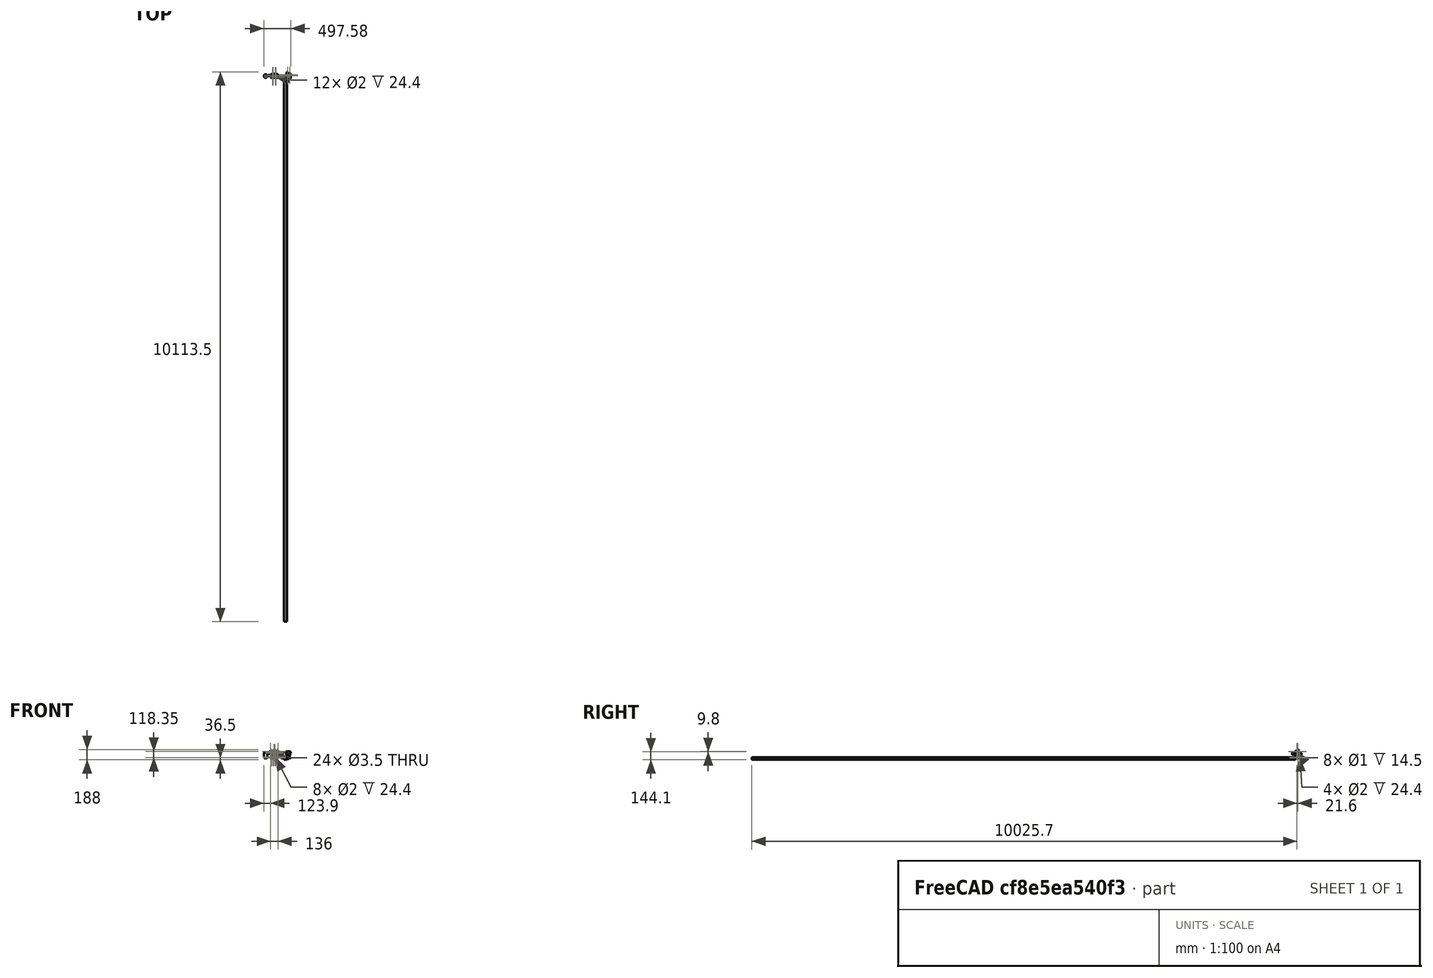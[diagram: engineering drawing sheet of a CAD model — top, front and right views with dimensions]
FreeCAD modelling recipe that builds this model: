
FCSTD DOCUMENT  (FreeCAD 0.15R4671 (Git))
Label: darth void
License: All rights reserved
LicenseURL: http://es.wikipedia.org/wiki/Todos_los_derechos_reservados
objects: Part::Feature×135, Part::Cylinder×55, Part::Cut×53, Part::Box×41, Part::MultiFuse×36, Sketcher::SketchObject×14, Part::FeaturePython×14, App::DocumentObjectGroup×10, Part::Mirroring×9, Part::Fillet×9, PartDesign::Pad×9, Part::Chamfer×6, PartDesign::Pocket×5, Part::Prism×3, Mesh::Feature×3, PartDesign::Fillet×2
note: 405 computed .brp shape members not serialized (recipe doc carries the construction recipe); baked Part::Feature solids carry a one-line shape summary decoded from their .brp

FEATURE [Part::Feature] Part__Feature  label="Servo-D1"
  Placement = pos=(26.5,9.5,100.6) rot=(0,1,0;3.14159rad)
  shape: bbox 55.5 x 20 x 41.74 mm, 365 faces (baked)
FEATURE [Part::Feature] Part__Feature001  label="Servo-D2"
  Placement = pos=(0,0,13) rot=(0.57735,0.57735,0.57735;2.0944rad)
  shape: bbox 41.74 x 55.5 x 20 mm, 365 faces (baked)
FEATURE [Part::Feature] Part__Feature002  label="J1"
  Placement = pos=(-10.8,44.37,77.54) rot=(0.707107,0.707107,0;3.14159rad)
  shape: bbox 11.7 x 15.49 x 2.5 mm, 224 faces (baked)
FEATURE [Part::Feature] Part__Feature003  label="J2"
  Placement = pos=(-10.8,62.15,77.54) rot=(0.707107,0.707107,0;3.14159rad)
  shape: bbox 11.7 x 15.49 x 2.5 mm, 224 faces (baked)
FEATURE [Part::Feature] Part__Feature004  label="J4"
  Placement = pos=(-10.8,59.6199,125.78) rot=(0,0,-1;1.5708rad)
  shape: bbox 11.65 x 20.57 x 2.5 mm, 290 faces (baked)
FEATURE [Part::Feature] Part__Feature005  label="J16"
  Placement = pos=(-9.55,7.19908,100.417) rot=(0.57735,0.57735,-0.57735;2.0944rad)
  shape: bbox 2.94 x 5.43 x 7.98 mm, 414 faces, 0 solids (baked)
FEATURE [Part::Feature] Part__Feature006  label="PCB"
  Placement = pos=(-12.3914,5,75) rot=(0.57735,0.57735,0.57735;2.0944rad)
  shape: bbox 1.591 x 68.6 x 53.36 mm, 426 faces (baked)
FEATURE [Part::Feature] Part__Feature007  label="J010"
  Placement = pos=(-10.8,14.8841,83.3059) rot=(0.707107,0.707107,0;3.14159rad)
  shape: bbox 10.92 x 14.61 x 8.89 mm, 41 faces (baked)
FEATURE [Part::Feature] Part__Feature008  label="U1"
  Placement = pos=(-9.2,12.159,115.511) rot=(0.57735,-0.57735,-0.57735;2.0944rad)
  shape: bbox 2.435 x 26.9 x 13 mm, 503 faces (baked)
FEATURE [Part::Feature] Part__Feature009  label="J8"
  Placement = pos=(-10.8,37.7759,125.78) rot=(0,0,-1;1.5708rad)
  shape: bbox 11.65 x 20.57 x 2.5 mm, 290 faces (baked)
FEATURE [App::DocumentObjectGroup] Group  label="placa"
  Group = -> [Part__Feature002,Part__Feature003,Part__Feature004,Part__Feature005,Part__Feature006,Part__Feature007,Part__Feature008,Part__Feature009]
FEATURE [Part::Box] Box  label="Cube"
  Height = 24
  Length = 72
  Placement = pos=(-15,-29,-3) rot=(0,0,1;0rad)
  Width = 58
FEATURE [Part::Box] Box001  label="Cube001"
  Height = 25
  Length = 47
  Placement = pos=(-1,-21,2) rot=(0,0,1;0rad)
  Width = 42
FEATURE [Part::Box] Box002  label="Cube002"
  Height = 38
  Length = 28
  Placement = pos=(37,-45,1) rot=(0,0,1;0rad)
  Width = 88
FEATURE [Part::Box] Box003  label="Cube003"
  Height = 38
  Length = 28
  Placement = pos=(-33,-45,1) rot=(0,0,1;0rad)
  Width = 88
FEATURE [Part::Cut] Cut
  Base = -> Box
  Tool = -> Box001
FEATURE [Part::Cut] Cut001
  Base = -> Cut
  Tool = -> Box002
FEATURE [Part::Cut] Cut002
  Base = -> Cut001
  Tool = -> Box003
FEATURE [Part::Box] Box004  label="Cube004"
  Height = 60
  Length = 44
  Placement = pos=(-5,-24,-5) rot=(0,0,1;0rad)
  Width = 61
FEATURE [Part::Mirroring] Part__Mirroring  label="Servo-D1 (Mirror #1)"
  Base = (0,0,0)
  Normal = (0,1,0)
  Placement = pos=(0,72,0) rot=(0,0,1;0rad)
  Source = -> Part__Feature
FEATURE [Part::Mirroring] Part__Mirroring001  label="Servo-D2 (Mirror #2)"
  Base = (0,0,0)
  Normal = (0,1,0)
  Placement = pos=(0,72,0) rot=(0,0,1;0rad)
  Source = -> Part__Feature001
FEATURE [Part::Cylinder] Cylinder  label="Joint-D005"
  Angle = 360
  Height = 74.5
  Placement = pos=(-22,9.5,12) rot=(0,1,0;1.5708rad)
  Radius = 1.75
FEATURE [Part::Fillet] Fillet
  Base = -> Cut002
  Edges = 4 edges r=10: [Edge1,Edge3,Edge5,Edge14]
FEATURE [Part::Cylinder] Cylinder001  label="Joint-D004"
  Angle = 360
  Height = 53
  Placement = pos=(-9,9.5,12) rot=(0,1,0;1.5708rad)
  Radius = 10.5
FEATURE [Part::MultiFuse] Fusion
  Shapes = -> [Cylinder001]
FEATURE [Part::Cylinder] Cylinder002  label="Joint-D006"
  Angle = 360
  Height = 74.5
  Placement = pos=(16,9.5,12) rot=(0,1,0;1.5708rad)
  Radius = 5.5
FEATURE [Part::Cut] Cut003
  Base = -> Fusion
  Tool = -> Box004
FEATURE [Part::Cylinder] Cylinder003  label="Joint-D007"
  Angle = 360
  Height = 74.5
  Placement = pos=(-51,9.5,12) rot=(0,1,0;1.5708rad)
  Radius = 1.75
FEATURE [Part::Cut] Cut004
  Base = -> Cut003
  Tool = -> Cylinder002
FEATURE [Part::Cut] Cut005
  Base = -> Cut004
  Tool = -> Cylinder003
FEATURE [Part::Cylinder] Cylinder004  label="Joint-D008"
  Angle = 360
  Height = 74.5
  Placement = pos=(41.8,9.5,12) rot=(0,1,0;1.5708rad)
  Radius = 11
FEATURE [Part::Cut] Cut006
  Base = -> Cut005
  Tool = -> Cylinder004
FEATURE [Part::Cylinder] Cylinder005  label="Joint-D009"
  Angle = 360
  Height = 23.5
  Placement = pos=(16.8,9.5,58.3) rot=(0,1,0;3.14159rad)
  Radius = 11
FEATURE [Part::Cylinder] Cylinder006  label="Joint-D010"
  Angle = 360
  Height = 21.5
  Placement = pos=(16,-24.5,7) rot=(0,1,0;1.5708rad)
  Radius = 1.75
FEATURE [Part::Cylinder] Cylinder007  label="Joint-D011"
  Angle = 360
  Height = 21.5
  Placement = pos=(32,-24.5,7) rot=(0,1,0;1.5708rad)
  Radius = 3
FEATURE [Part::MultiFuse] Fusion001
  Shapes = -> [Cylinder007,Cylinder006]
FEATURE [Part::MultiFuse] Fusion002
  Placement = pos=(0,0,10) rot=(0,0,1;0rad)
  Shapes = -> [Cylinder007,Cylinder006]
FEATURE [Part::MultiFuse] Fusion003
  Placement = pos=(0,49,0) rot=(0,0,1;0rad)
  Shapes = -> [Cylinder007,Cylinder006]
FEATURE [Part::MultiFuse] Fusion004
  Placement = pos=(0,49,10) rot=(0,0,1;0rad)
  Shapes = -> [Cylinder007,Cylinder006]
FEATURE [Part::Box] Box005  label="Cube006"
  Height = 21
  Length = 4
  Placement = pos=(25.5,-28,2) rot=(0,0,1;0rad)
  Width = 56
FEATURE [Part::Cylinder] Cylinder008  label="Joint-D012"
  Angle = 360
  Height = 74.5
  Placement = pos=(17,9.5,12) rot=(0,0,1;0rad)
  Radius = 5.5
FEATURE [Part::Box] Box006  label="Cube007"
  Height = 6
  Length = 3
  Placement = pos=(18.5,-28,4) rot=(0,0,1;0rad)
  Width = 56
FEATURE [Part::Box] Box007  label="Cube008"
  Height = 6
  Length = 3
  Placement = pos=(18.5,-28,14) rot=(0,0,1;0rad)
  Width = 56
FEATURE [Part::Cylinder] Cylinder009  label="Joint-D013"
  Angle = 360
  Height = 74.5
  Placement = pos=(-3,9.5,12) rot=(0,1,0;1.5708rad)
  Radius = 2.75
FEATURE [Part::Box] Box008  label="Cube009"
  Height = 5
  Length = 80
  Placement = pos=(-23,-4,63) rot=(0,0,1;0rad)
  Width = 80
FEATURE [Part::Box] Box009  label="Cube010"
  Height = 9
  Length = 7
  Placement = pos=(-1,-1,63) rot=(0,0,1;0rad)
  Width = 74
FEATURE [Part::Box] Box010  label="Cube011"
  Height = 9
  Length = 7
  Placement = pos=(47,-1,63) rot=(0,0,1;0rad)
  Width = 74
FEATURE [Part::MultiFuse] Fusion005
  Placement = pos=(44,39,98) rot=(0,1,0;1.5708rad)
  Shapes = -> [Cylinder007,Cylinder006]
FEATURE [Part::MultiFuse] Fusion006
  Placement = pos=(44,29,98) rot=(0,1,0;1.5708rad)
  Shapes = -> [Cylinder007,Cylinder006]
FEATURE [Part::MultiFuse] Fusion007
  Placement = pos=(-5,39,98) rot=(0,1,0;1.5708rad)
  Shapes = -> [Cylinder007,Cylinder006]
FEATURE [Part::MultiFuse] Fusion008
  Placement = pos=(-5,29,98) rot=(0,1,0;1.5708rad)
  Shapes = -> [Cylinder007,Cylinder006]
FEATURE [Part::Box] Box011  label="Cube012"
  Height = 9
  Length = 70
  Placement = pos=(-6,8.5,70) rot=(0,0,1;0rad)
  Width = 2
FEATURE [Part::MultiFuse] Fusion009
  Shapes = -> [Box011,Fusion007,Fusion008,Fusion006,Fusion005]
FEATURE [Part::MultiFuse] Fusion010
  Placement = pos=(0,53,0) rot=(0,0,1;0rad)
  Shapes = -> [Box011,Fusion007,Fusion008,Fusion006,Fusion005]
FEATURE [Part::MultiFuse] Fusion011
  Shapes = -> [Box008,Box010,Box009]
FEATURE [Part::Cut] Cut016
  Base = -> Fusion011
  Tool = -> Fusion010
FEATURE [Part::Cut] Cut017
  Base = -> Cut016
  Tool = -> Fusion009
FEATURE [Part::Box] Box012  label="Cube014"
  Height = 43
  Length = 41
  Placement = pos=(6,-1,59) rot=(0,0,1;0rad)
  Width = 21
FEATURE [Part::Box] Box013  label="Cube015"
  Height = 43
  Length = 41
  Placement = pos=(6,52,59) rot=(0,0,1;0rad)
  Width = 21
FEATURE [Part::Cut] Cut018
  Base = -> Cut017
  Tool = -> Box012
FEATURE [Part::Cut] Cut019
  Base = -> Cut018
  Tool = -> Box013
FEATURE [Part::Box] Box014  label="Cube016"
  Height = 12
  Length = 6
  Placement = pos=(-11.5,3,69) rot=(0,0,1;0rad)
  Width = 3
FEATURE [Part::Box] Box015  label="Cube017"
  Height = 12
  Length = 16
  Placement = pos=(-20,-1,63) rot=(0,0,1;0rad)
  Width = 74
FEATURE [Part::Box] Box016  label="Cube018"
  Height = 12
  Length = 6
  Placement = pos=(-11.5,66,69) rot=(0,0,1;0rad)
  Width = 3
FEATURE [Part::MultiFuse] Fusion012
  Shapes = -> [Cut019,Box015]
FEATURE [Part::Cut] Cut020
  Base = -> Fusion012
  Tool = -> Box014
FEATURE [Part::Cut] Cut021
  Base = -> Cut020
  Tool = -> Box016
FEATURE [PartDesign::Fillet] Fillet001  label="horn"
  Placement = pos=(38.5,9.5,13) rot=(0,0,-1;1.5708rad)
  Radius = 0.5
FEATURE [Part::Cylinder] Cylinder010  label="Joint-D014"
  Angle = 360
  Height = 52.5
  Placement = pos=(19,9.5,20.35) rot=(0,1,0;1.5708rad)
  Radius = 1
FEATURE [Part::Cylinder] Cylinder011  label="Joint-D015"
  Angle = 360
  Height = 52.5
  Placement = pos=(19,2,9.5) rot=(0,1,0;1.5708rad)
  Radius = 1
FEATURE [Part::Cylinder] Cylinder012  label="Joint-D016"
  Angle = 360
  Height = 52.5
  Placement = pos=(19,17,9.5) rot=(0,1,0;1.5708rad)
  Radius = 1
FEATURE [Part::MultiFuse] Fusion013
  Placement = pos=(0,0,-1) rot=(0,0,1;0rad)
  Shapes = -> [Cylinder011,Cylinder010,Cylinder012]
FEATURE [Part::MultiFuse] Fusion014
  Placement = pos=(4,0,101) rot=(0,1,0;1.5708rad)
  Shapes = -> [Cylinder011,Cylinder010,Cylinder012]
FEATURE [PartDesign::Fillet] Fillet002  label="horn001"
  Placement = pos=(16.8,9.5,62.5) rot=(-0.57735,0.57735,-0.57735;2.0944rad)
  Radius = 0.5
FEATURE [Part::Mirroring] Part__Mirroring002  label="horn (Mirror #4)"
  Base = (41.6,1.90735e-06,13)
  Normal = (0,1,-1.19209e-07)
  Placement = pos=(0,72,0) rot=(0,0,1;0rad)
  Source = -> Fillet001
FEATURE [Part::Mirroring] Part__Mirroring003  label="horn001 (Mirror #5)"
  Base = (16.8,7.62939e-06,59.3998)
  Normal = (0,1,-1.19209e-07)
  Placement = pos=(0,72,0) rot=(0,0,1;0rad)
  Source = -> Fillet002
FEATURE [Part::Chamfer] Chamfer
  Base = -> Fillet
  Edges = 3 edges r=3: [Edge18,Edge33,Edge37]
FEATURE [Part::Cut] Cut007
  Base = -> Chamfer
  Tool = -> Cylinder
FEATURE [Part::Cut] Cut008
  Base = -> Cut007
  Tool = -> Box005
FEATURE [Part::Cut] Cut009
  Base = -> Cut008
  Tool = -> Box007
FEATURE [Part::Cut] Cut010
  Base = -> Cut009
  Tool = -> Box006
FEATURE [Part::Cut] Cut011
  Base = -> Cut010
  Tool = -> Fusion004
FEATURE [Part::Cut] Cut012
  Base = -> Cut011
  Tool = -> Fusion003
FEATURE [Part::Cut] Cut013
  Base = -> Cut012
  Tool = -> Fusion002
FEATURE [Part::Cut] Cut014
  Base = -> Cut013
  Tool = -> Fusion001
FEATURE [Part::Cut] Cut015  label="pie"
  Base = -> Cut014
  Tool = -> Cylinder009
FEATURE [Part::Box] Box017  label="Cube024"
  Height = 23
  Length = 6
  Placement = pos=(0,19,7) rot=(0,0,1;0rad)
  Width = 36
FEATURE [Part::Cut] Cut022  label="pie-D"
  Base = -> Cut015
  Placement = pos=(0,0,1) rot=(0,0,1;0rad)
  Tool = -> Box017
FEATURE [Part::Mirroring] Part__Mirroring004  label="pie-I"
  Base = (0,0,0)
  Normal = (0,1,0)
  Placement = pos=(0,72,0) rot=(0,0,1;0rad)
  Source = -> Cut022
FEATURE [Part::Cut] Cut023
  Base = -> Cut006
  Tool = -> Box004
FEATURE [Part::Cut] Cut024
  Base = -> Cut023
  Tool = -> Cylinder005
FEATURE [Part::Cut] Cut025
  Base = -> Cut024
  Tool = -> Fusion014
FEATURE [Part::Cut] Cut026
  Base = -> Cut025
  Tool = -> Fusion013
FEATURE [Part::Cut] Cut027
  Base = -> Cut026
  Placement = pos=(0,0,1) rot=(0,0,1;0rad)
  Tool = -> Cylinder008
FEATURE [Part::Chamfer] Chamfer001
  Base = -> Cut027
  Edges = 1 edges r=4: [Edge61]
FEATURE [Part::Chamfer] Chamfer002  label="pata-D"
  Base = -> Chamfer001
  Edges = 1 edges r=8: [Edge58]
FEATURE [Part::Mirroring] Part__Mirroring005  label="pata-I"
  Base = (17.5,3.8147e-06,32.25)
  Normal = (0,1,-1.19209e-07)
  Placement = pos=(0,72,0) rot=(0,0,1;0rad)
  Source = -> Chamfer002
FEATURE [Part::Cylinder] Cylinder013  label="Cylinder055"
  Angle = 360
  Height = 31
  Placement = pos=(-8.5,92,71.5) rot=(1,0,0;1.5708rad)
  Radius = 1.75
FEATURE [Part::Cut] Cut028
  Base = -> Cut021
  Tool = -> Cylinder013
FEATURE [Part::Cylinder] Cylinder014  label="Cylinder001"
  Angle = 360
  Height = 31
  Placement = pos=(-8.5,11,71.5) rot=(1,0,0;1.5708rad)
  Radius = 1.75
FEATURE [Part::Feature] Part__Feature010  label="Portapilas008"
  shape: bbox 2e-07 x 47.97 x 51.59 mm, 1 faces, 0 solids (baked)
FEATURE [Part::Feature] Part__Feature011  label="Portapilas007"
  shape: bbox 9.213 x 1.1 x 48.01 mm, 3 faces, 0 solids (baked)
FEATURE [Part::Feature] Part__Feature012  label="Portapilas006"
  shape: bbox 9.213 x 1.1 x 48.01 mm, 3 faces, 0 solids (baked)
FEATURE [Part::Feature] Part__Feature013  label="Portapilas005"
  shape: bbox 9.213 x 1.1 x 48.01 mm, 3 faces, 0 solids (baked)
FEATURE [Part::Feature] Part__Feature014  label="Portapilas004"
  shape: bbox 9.213 x 1.1 x 48.01 mm, 3 faces, 0 solids (baked)
FEATURE [Part::Feature] Part__Feature015  label="Portapilas003"
  shape: bbox 9.213 x 1.1 x 48.01 mm, 3 faces, 0 solids (baked)
FEATURE [Part::Feature] Part__Feature016  label="Portapilas002"
  shape: bbox 9.213 x 1.1 x 48.01 mm, 3 faces, 0 solids (baked)
FEATURE [Part::Feature] Part__Feature017  label="Portapilas001"
  shape: bbox 16.42 x 48.04 x 51.59 mm, 26 faces, 0 solids (baked)
FEATURE [Part::Feature] Part__Feature018  label="Portapilas"
  shape: bbox 21.03 x 69.14 x 72.63 mm, 394 faces, 0 solids (baked)
FEATURE [Part::MultiFuse] Fusion015  label="peterpilas"
  Placement = pos=(23,77.5,76) rot=(0,0,1;1.5708rad)
  Shapes = -> [Part__Feature018,Part__Feature017,Part__Feature016,Part__Feature015,Part__Feature014,Part__Feature013,Part__Feature012,Part__Feature011,Part__Feature010]
FEATURE [Part::Feature] Part__Feature019  label="Ultrasonido_BAT"
  Placement = pos=(-17,36,59.5) rot=(0,0,1;0rad)
  shape: bbox 18.72 x 56 x 27.52 mm, 81 faces (baked)
FEATURE [Part::Cut] Cut029
  Base = -> Cut028
  Tool = -> Cylinder014
FEATURE [Part::Box] Box018  label="Cube032"
  Height = 20
  Length = 3
  Placement = pos=(51,20,66) rot=(0,0,1;0rad)
  Width = 32
FEATURE [Part::Box] Box019  label="Cube033"
  Height = 54
  Length = 4.5
  Placement = pos=(-20,6,64) rot=(0,0,1;0rad)
  Width = 60
FEATURE [Part::Box] Box020  label="Cube035"
  Height = 68
  Length = 6
  Placement = pos=(-23.5,17,68) rot=(0,0,1;0rad)
  Width = 38
FEATURE [Part::Box] Box021  label="Cube034"
  Height = 17
  Length = 13
  Placement = pos=(-14,20,62) rot=(0,0,1;0rad)
  Width = 32
FEATURE [Part::Fillet] Fillet003
  Base = -> Box021
  Edges = 4 edges r=5: [Edge1,Edge3,Edge5,Edge7]
FEATURE [Part::Cylinder] Cylinder015  label="Cylinder093"
  Angle = 360
  Height = 31
  Placement = pos=(-49.5,29,111.5) rot=(0,1,0;1.5708rad)
  Radius = 1.75
FEATURE [Part::Cylinder] Cylinder016  label="Cylinder094"
  Angle = 360
  Height = 31
  Placement = pos=(-49.5,49,91.5) rot=(0,1,0;1.5708rad)
  Radius = 1.75
FEATURE [Part::Cylinder] Cylinder017  label="Cylinder095"
  Angle = 360
  Height = 31
  Placement = pos=(-49.5,49,111.5) rot=(0,1,0;1.5708rad)
  Radius = 1.75
FEATURE [Part::MultiFuse] Fusion016
  Shapes = -> [Box018,Cut029]
FEATURE [Part::Box] Box022  label="Cube036"
  Height = 44
  Length = 61
  Placement = pos=(-9,22,66) rot=(0,0,1;0rad)
  Width = 28
FEATURE [Part::MultiFuse] Fusion017
  Shapes = -> [Fusion016,Box019]
FEATURE [Part::Cut] Cut030
  Base = -> Fusion017
  Tool = -> Fillet003
FEATURE [Part::Box] Box023  label="Cube037"
  Height = 11
  Length = 8
  Placement = pos=(-11.5,-52,95) rot=(0,0,1;0rad)
  Width = 58
FEATURE [Part::Cylinder] Cylinder018  label="Cylinder096"
  Angle = 360
  Height = 61
  Placement = pos=(-5,124,89.6) rot=(1,0,0;1.5708rad)
  Radius = 4
FEATURE [Part::Cylinder] Cylinder019  label="Cylinder097"
  Angle = 360
  Height = 63
  Placement = pos=(-3,11,83.5) rot=(1,0,0;1.5708rad)
  Radius = 6
FEATURE [Part::Box] Box024  label="Cube038"
  Height = 66
  Length = 76
  Placement = pos=(-21,-2,63) rot=(0,0,1;0rad)
  Width = 76
FEATURE [Part::Cylinder] Cylinder020  label="Cylinder098"
  Angle = 360
  Height = 23
  Placement = pos=(-8.5,1,71.5) rot=(1,0,0;1.5708rad)
  Radius = 1.75
FEATURE [Part::Cylinder] Cylinder021  label="Cylinder099"
  Angle = 360
  Height = 31
  Placement = pos=(-8.5,94,71.5) rot=(1,0,0;1.5708rad)
  Radius = 1.75
FEATURE [Part::Fillet] Fillet004
  Base = -> Box024
  Edges = 8 edges r=3: [Edge1,Edge2,Edge3,Edge5,Edge6,Edge7,Edge10,Edge12]
FEATURE [Part::Box] Box025  label="Cube039"
  Height = 6
  Length = 81
  Placement = pos=(-23.5,-4.5,63) rot=(0,0,1;0rad)
  Width = 81
FEATURE [Part::Fillet] Fillet005
  Base = -> Box025
  Edges = 4 edges r=5: [Edge1,Edge3,Edge5,Edge7]
  Placement = pos=(0,0,-1) rot=(0,0,1;0rad)
FEATURE [Part::Cylinder] Cylinder022  label="Cylinder100"
  Angle = 360
  Height = 45
  Placement = pos=(-8.5,-7,71.5) rot=(1,0,0;1.5708rad)
  Radius = 4
FEATURE [Part::Cylinder] Cylinder023  label="Cylinder101"
  Angle = 360
  Height = 45
  Placement = pos=(-8.5,124,71.5) rot=(1,0,0;1.5708rad)
  Radius = 4
FEATURE [Part::MultiFuse] Fusion018
  Shapes = -> [Fillet004,Fillet005]
FEATURE [Part::MultiFuse] Fusion019  label="corte-positivo"
  Shapes = -> [Fusion018,Cylinder018,Cylinder023,Cylinder021,Cylinder022,Cylinder019,Box023,Cylinder020]
FEATURE [Part::Cylinder] Cylinder024  label="Cylinder102"
  Angle = 360
  Height = 31
  Placement = pos=(-49.5,29,91.5) rot=(0,1,0;1.5708rad)
  Radius = 1.75
FEATURE [Part::MultiFuse] Fusion020
  Placement = pos=(14,0,0) rot=(0,0,1;0rad)
  Shapes = -> [Cylinder024,Cylinder016,Cylinder017,Cylinder015]
FEATURE [App::DocumentObjectGroup] Group002  label="electronic"
  Group = -> [Part__Mirroring,Part__Mirroring001,Part__Mirroring002,Part__Mirroring003,Fusion015,Part__Feature019,Group]
FEATURE [App::DocumentObjectGroup] Group003  label="aux"
  Group = -> [Fusion019]
FEATURE [Part::Cut] Cut031
  Base = -> Cut030
  Tool = -> Box022
FEATURE [Part::Chamfer] Chamfer003
  Base = -> Cut031
  Edges = 1 edges r=3: [Edge86]
FEATURE [Sketcher::SketchObject] Sketch
  Placement = pos=(-22,0,0) rot=(0.57735,-0.57735,-0.57735;2.0944rad)
  sketch-geometry (4):
    g0: ArcOfCircle CenterX=-49 CenterY=111.5 CenterZ=0 NormalX=0 NormalY=0 NormalZ=1 Radius=3.5 StartAngle=9.1497e-08 EndAngle=3.14159
    g1: LineSegment StartX=-52.5 StartY=111.5 StartZ=0 EndX=-52.5 EndY=91.5 EndZ=0
    g2: LineSegment StartX=-45.5 StartY=111.5 StartZ=0 EndX=-45.5 EndY=91.5 EndZ=0
    g3: ArcOfCircle CenterX=-49 CenterY=91.5 CenterZ=0 NormalX=0 NormalY=0 NormalZ=1 Radius=3.5 StartAngle=3.14159 EndAngle=6.28319
  constraints (13):
    c: DistanceX(g-1,g0) = -49
    c: DistanceY(g-1,g0) = 111.5
    c: Radius(g0) = 3.5
    c: Vertical(g1)
    c: Vertical(g2)
    c: Coincident(g1,g0)
    c: Coincident(g2,g0)
    c: Tangent(g2,g0)
    c: Tangent(g1,g0)
    c: Coincident(g3,g1)
    c: Coincident(g3,g2)
    c: Equal(g3,g0)
    c: Distance(g3,g0) = 20
FEATURE [PartDesign::Pad] Pad
  Length = 5
  Length2 = 100
  Placement = pos=(-22,0,0) rot=(0.57735,-0.57735,-0.57735;2.0944rad)
  Reversed = true
  Sketch = -> Sketch
  Type = 0
FEATURE [Part::FeaturePython] Clone001  label="Clone of Pad"  # Draft clone (typed FeaturePython)
  Objects = -> [Pad]
  Placement = pos=(-22,-20,0) rot=(0.57735,-0.57735,-0.57735;2.0944rad)
  Scale = (1,1,1)
FEATURE [Part::MultiFuse] Fusion021
  Placement = pos=(4.5,0,0) rot=(0,0,1;0rad)
  Shapes = -> [Pad,Clone001]
FEATURE [Part::MultiFuse] Fusion022
  Shapes = -> [Chamfer003,Fusion021]
FEATURE [Part::Cut] Cut032
  Base = -> Fusion022
  Tool = -> Fusion020
FEATURE [Part::Cut] Cut033
  Base = -> Cut032
  Tool = -> Box020
FEATURE [Sketcher::SketchObject] Sketch001  label="leg-sketch-1"
  Placement = pos=(0,0,0) rot=(0.57735,0.57735,0.57735;2.0944rad)
  sketch-geometry (5):
    g0: LineSegment StartX=-49 StartY=10.5 StartZ=0 EndX=0 EndY=10.5 EndZ=0
    g1: LineSegment StartX=0 StartY=10.5 StartZ=0 EndX=0 EndY=-10.5 EndZ=0
    g2: LineSegment StartX=0 StartY=-10.5 StartZ=0 EndX=-49 EndY=-10.5 EndZ=0
    g3: LineSegment [constr] StartX=-49 StartY=-10.5 StartZ=0 EndX=-49 EndY=10.5 EndZ=0
    g4: ArcOfCircle CenterX=-49 CenterY=0 CenterZ=0 NormalX=0 NormalY=0 NormalZ=1 Radius=10.5 StartAngle=1.5708 EndAngle=4.71239
  constraints (15):
    c: Coincident(g0,g1)
    c: Coincident(g1,g2)
    c: Coincident(g2,g3)
    c: Coincident(g3,g0)
    c: Horizontal(g0)
    c: Horizontal(g2)
    c: Vertical(g1)
    c: Vertical(g3)
    c: PointOnObject(g4,g3)
    c: Coincident(g4,g0)
    c: Coincident(g4,g2)
    c: PointOnObject(g4,g-1)
    c: PointOnObject(g0,g-2)
    c: DistanceX(g0) = 49
    c: DistanceY(g1) = -21
FEATURE [PartDesign::Pad] Pad001  label="leg-block-1"
  Length = 53
  Length2 = 100
  Midplane = true
  Placement = pos=(0,0,0) rot=(0.57735,0.57735,0.57735;2.0944rad)
  Sketch = -> Sketch001
  Type = 0
FEATURE [Sketcher::SketchObject] Sketch002  label="leg-top-sketch"
  ExternalGeometry = -> [Pad001]
  Placement = pos=(0,0,10.5) rot=(0,0,-1;1.5708rad)
  Support = -> Pad001 [Face1]
  sketch-geometry (9):
    g0: LineSegment StartX=64 StartY=21.5 StartZ=0 EndX=10 EndY=21.5 EndZ=0
    g1: LineSegment StartX=6 StartY=17.5 StartZ=0 EndX=6 EndY=-19.5 EndZ=0
    g2: LineSegment StartX=9 StartY=-22.5 StartZ=0 EndX=64 EndY=-22.5 EndZ=0
    g3: LineSegment StartX=64 StartY=-22.5 StartZ=0 EndX=64 EndY=21.5 EndZ=0
    g4: LineSegment StartX=6 StartY=17.5 StartZ=0 EndX=10 EndY=21.5 EndZ=0
    g5: LineSegment [constr] StartX=6 StartY=17.5 StartZ=0 EndX=6 EndY=21.5 EndZ=0
    g6: LineSegment StartX=6 StartY=-19.5 StartZ=0 EndX=9 EndY=-22.5 EndZ=0
    g7: LineSegment [constr] StartX=9 StartY=-22.5 StartZ=0 EndX=6 EndY=-22.5 EndZ=0
    g8: LineSegment [constr] StartX=6 StartY=-22.5 StartZ=0 EndX=6 EndY=-19.5 EndZ=0
  constraints (26):
    c: Coincident(g2,g3)
    c: Coincident(g3,g0)
    c: Horizontal(g0)
    c: Horizontal(g2)
    c: Vertical(g1)
    c: Vertical(g3)
    c: DistanceY(g-3,g5) = -5
    c: DistanceY(g7,g-4) = -4
    c: Angle(g-2,g4) = 2.35619
    c: Coincident(g1,g4)
    c: Coincident(g5,g1)
    c: Vertical(g5)
    c: DistanceY(g1,g7) = -40
    c: DistanceX(g5,g-3) = -6
    c: Coincident(g0,g4)
    c: PointOnObject(g5,g0)
    c: DistanceX(g-3,g0) = 15
    c: Coincident(g2,g6)
    c: Coincident(g7,g2)
    c: Horizontal(g7)
    c: DistanceX(g7) = -3
    c: Coincident(g1,g6)
    c: Coincident(g8,g7)
    c: Coincident(g8,g1)
    c: Equal(g8,g7)
    c: Vertical(g8)
FEATURE [PartDesign::Pocket] Pocket  label="leg-block-2"
  Length = 5
  Placement = pos=(0,0,0) rot=(0.57735,0.57735,0.57735;2.0944rad)
  Sketch = -> Sketch002
  Type = 1
FEATURE [Sketcher::SketchObject] Sketch003  label="ankle-rounded-horn-sketch"
  ExternalGeometry = -> [Pocket]
  Placement = pos=(26.5,0,0) rot=(0.57735,0.57735,0.57735;2.0944rad)
  Support = -> Pocket [Face4]
  sketch-geometry (1):
    g0: Circle CenterX=-49 CenterY=0 CenterZ=0 NormalX=0 NormalY=0 NormalZ=1 Radius=10.75
  constraints (2):
    c: Coincident(g0,g-3)
    c: Radius(g0) = 10.75
FEATURE [PartDesign::Pocket] Pocket001  label="ankle-rounded-horn-cutout"
  Length = 2.2
  Placement = pos=(0,0,0) rot=(0.57735,0.57735,0.57735;2.0944rad)
  Sketch = -> Sketch003
  Type = 0
FEATURE [Sketcher::SketchObject] Sketch004  label="ankle-rear-shaft-drill-sketch"
  ExternalGeometry = -> [Pocket001]
  Placement = pos=(-26.5,0,0) rot=(0.57735,0.57735,-0.57735;4.18879rad)
  Support = -> Pocket001 [Face2]
  sketch-geometry (1):
    g0: Circle CenterX=-49 CenterY=0 CenterZ=0 NormalX=0 NormalY=0 NormalZ=1 Radius=1.75
  constraints (2):
    c: Coincident(g0,g-3)
    c: Radius(g0) = 1.75
FEATURE [PartDesign::Pocket] Pocket002  label="ankle-rear-shaft-drill"
  Length = 0
  Placement = pos=(0,0,0) rot=(0.57735,0.57735,0.57735;2.0944rad)
  Sketch = -> Sketch004
  Type = 2
FEATURE [Sketcher::SketchObject] Sketch005  label="hip-rounded-horn-cutout-sketch"
  Placement = pos=(0,-6,0) rot=(-0.57735,-0.57735,0.57735;4.18879rad)
  Support = -> Pocket002 [Face10]
  sketch-geometry (1):
    g0: Circle CenterX=0 CenterY=0 CenterZ=0 NormalX=0 NormalY=0 NormalZ=1 Radius=11
  constraints (2):
    c: Coincident(g0,g-1)
    c: Radius(g0) = 11
FEATURE [PartDesign::Pocket] Pocket003  label="hip-rounded-horn-cutout"
  Length = 3.3
  Placement = pos=(0,0,0) rot=(0.57735,0.57735,0.57735;2.0944rad)
  Sketch = -> Sketch005
  Type = 0
FEATURE [Sketcher::SketchObject] Sketch006  label="horn-side-chamfer-sketch"
  ExternalGeometry = -> [Pocket003]
  Placement = pos=(0,0,10.5) rot=(0,0,-1;1.5708rad)
  Support = -> Pocket003 [Face1]
  sketch-geometry (3):
    g0: LineSegment StartX=0 StartY=18.5 StartZ=0 EndX=8 EndY=26.5 EndZ=0
    g1: LineSegment StartX=0 StartY=18.5 StartZ=0 EndX=0 EndY=26.5 EndZ=0
    g2: LineSegment StartX=0 StartY=26.5 StartZ=0 EndX=8 EndY=26.5 EndZ=0
  constraints (8):
    c: PointOnObject(g0,g-2)
    c: PointOnObject(g0,g-3)
    c: Angle(g-2,g0) = 2.35619
    c: DistanceY(g-3,g0) = -8
    c: Coincident(g0,g1)
    c: Coincident(g1,g-3)
    c: Coincident(g1,g2)
    c: Coincident(g2,g0)
FEATURE [PartDesign::Pocket] Pocket004  label="horn-side-chamfer"
  Length = 5
  Placement = pos=(0,0,0) rot=(0.57735,0.57735,0.57735;2.0944rad)
  Sketch = -> Sketch006
  Type = 1
FEATURE [Part::Cylinder] Cylinder025  label="servo-shaft-drill"
  Angle = 360
  Height = 20
  Placement = pos=(0,10,0) rot=(1,0,0;1.5708rad)
  Radius = 5.5
FEATURE [Part::Cylinder] Cylinder026  label="servo-horn-small-drill-master"
  Angle = 360
  Height = 20
  Placement = pos=(-3.5,10,7.5) rot=(1,0,0;1.5708rad)
  Radius = 1
FEATURE [Part::FeaturePython] Clone002  label="Clone of servo-horn-small-drill-master"  # Draft clone (typed FeaturePython)
  Objects = -> [Cylinder026]
  Placement = pos=(7.35,10,-2.33815e-06) rot=(1,0,0;1.5708rad)
  Scale = (1,1,1)
FEATURE [Part::FeaturePython] Clone003  label="Clone of servo-horn-small-drill-master001"  # Draft clone (typed FeaturePython)
  Objects = -> [Cylinder026]
  Placement = pos=(-3.5,10,-7.5) rot=(1,0,0;1.5708rad)
  Scale = (1,1,1)
FEATURE [Part::MultiFuse] Fusion023  label="servo-Drills-block1-master"
  Shapes = -> [Clone002,Clone003,Cylinder026,Cylinder025]
FEATURE [Part::FeaturePython] Clone004  label="Clone of servo-Drills-block1-master"  # Draft clone (typed FeaturePython)
  Objects = -> [Fusion023]
  Placement = pos=(22,-49,6.96015e-06) rot=(0,0,1;1.5708rad)
  Scale = (1,1,1)
FEATURE [Part::MultiFuse] Fusion024  label="Servo-horn-drills"
  Shapes = -> [Fusion023,Clone004]
FEATURE [Part::Cut] Cut034  label="Leg"
  Base = -> Pocket004
  Tool = -> Fusion024
FEATURE [App::DocumentObjectGroup] Group005  label="Leg-src"
  Group = -> [Pad001,Pocket,Pocket001,Pocket002,Pocket003,Cut034]
FEATURE [App::DocumentObjectGroup] Group004  label="src"
  Group = -> [Group005]
FEATURE [Part::Feature] Fusion025  label="soft-drink-can"
  Placement = pos=(-397.85,47.19,0) rot=(0,0,-1;1.5708rad)
  shape: bbox 66.1 x 66.1 x 115.2 mm, 53 faces (baked)
FEATURE [App::DocumentObjectGroup] Group007  label="development"
  Group = -> [Group004]
FEATURE [Part::Fillet] Fillet006  label="chass"
  Base = -> Cut033
  Edges = 4 edges r=3: [Edge75,Edge118,Edge216,Edge229]
FEATURE [Sketcher::SketchObject] Sketch007
  Placement = pos=(-1,0,0) rot=(0.57735,0.57735,0.57735;2.0944rad)
  sketch-geometry (5):
    g0: LineSegment StartX=-35.7295 StartY=116.767 StartZ=0 EndX=-15.7739 EndY=107.988 EndZ=0
    g1: LineSegment StartX=-7.00034 StartY=107.988 StartZ=0 EndX=-7.00034 EndY=136.643 EndZ=0
    g2: LineSegment StartX=-7.00034 StartY=136.643 StartZ=0 EndX=-31.551 EndY=136.643 EndZ=0
    g3: ArcOfCircle CenterX=-31.551 CenterY=126.266 CenterZ=0 NormalX=0 NormalY=0 NormalZ=1 Radius=10.3774 StartAngle=1.5708 EndAngle=4.29797
    g4: LineSegment StartX=-15.7739 StartY=107.988 StartZ=0 EndX=-7.00034 EndY=107.988 EndZ=0
  constraints (10):
    c: Coincident(g1,g2)
    c: Coincident(g2,g3)
    c: Coincident(g0,g3)
    c: Horizontal(g2)
    c: Vertical(g1)
    c: Tangent(g3,g0)
    c: Tangent(g3,g2)
    c: Coincident(g1,g4)
    c: Coincident(g0,g4)
    c: Horizontal(g4)
FEATURE [PartDesign::Pad] Pad002
  Length = 42
  Length2 = 100
  Placement = pos=(-1,0,0) rot=(0.57735,0.57735,0.57735;2.0944rad)
  Sketch = -> Sketch007
  Type = 0
FEATURE [Part::MultiFuse] Fusion026  label="servo-src"
  Placement = pos=(23,4.5,120) rot=(0,0.707107,-0.707107;3.14159rad)
  Shapes = -> [Part__Feature010,Part__Feature007,Part__Feature006]
FEATURE [Part::FeaturePython] Clone005  label="microservo"  # Draft clone (typed FeaturePython)
  Objects = -> [Fusion026]
  Placement = pos=(-207.5,47,122.5) rot=(0.57735,0.57735,0.57735;2.0944rad)
  Scale = (1,1,1)
FEATURE [Part::FeaturePython] Clone006  label="microservo001"  # Draft clone (typed FeaturePython)
  Objects = -> [Fusion026]
  Placement = pos=(-270.5,47,122.5) rot=(0.57735,0.57735,-0.57735;4.18879rad)
  Scale = (1,1,1)
FEATURE [Part::FeaturePython] Clone007  label="microservo002"  # Draft clone (typed FeaturePython)
  Objects = -> [Fusion026]
  Placement = pos=(-307,51.5,122.5) rot=(0.57735,-0.57735,0.57735;2.0944rad)
  Scale = (1,1,1)
FEATURE [Sketcher::SketchObject] Sketch008
  Placement = pos=(3,-12,-1) rot=(0.57735,0.57735,0.57735;2.0944rad)
  sketch-geometry (4):
    g0: LineSegment StartX=-4.88207 StartY=101.941 StartZ=0 EndX=-4.88207 EndY=138.56 EndZ=0
    g1: LineSegment StartX=-4.88207 StartY=138.56 StartZ=0 EndX=-40.5711 EndY=142.374 EndZ=0
    g2: LineSegment StartX=-40.5711 StartY=142.374 StartZ=0 EndX=-40.5711 EndY=120.688 EndZ=0
    g3: LineSegment StartX=-40.5711 StartY=120.688 StartZ=0 EndX=-4.88207 EndY=101.941 EndZ=0
  constraints (6):
    c: Coincident(g0,g1)
    c: Coincident(g1,g2)
    c: Coincident(g2,g3)
    c: Coincident(g0,g3)
    c: Vertical(g0)
    c: Vertical(g2)
FEATURE [PartDesign::Pad] Pad003
  Length = 34
  Length2 = 100
  Placement = pos=(3,-12,-1) rot=(0.57735,0.57735,0.57735;2.0944rad)
  Sketch = -> Sketch008
  Type = 0
FEATURE [Part::Cut] Cut035
  Base = -> Pad002
  Tool = -> Pad003
FEATURE [Part::Cylinder] Cylinder027  label="Cilindro"
  Angle = 360
  Height = 10
  Placement = pos=(17.25,-4,120) rot=(1,0,0;1.5708rad)
  Radius = 10
FEATURE [Part::Cut] Cut036
  Base = -> Cut035
  Tool = -> Cylinder027
FEATURE [Part::Cylinder] Cylinder028  label="Cilindro001"
  Angle = 360
  Height = 13
  Placement = pos=(17.25,-6,120) rot=(1,0,0;1.5708rad)
  Radius = 3
FEATURE [Part::Cut] Cut037
  Base = -> Cut036
  Tool = -> Cylinder028
FEATURE [Part::Chamfer] Chamfer004
  Base = -> Cut037
  Edges = 1 edges r=1: [Edge10]
FEATURE [Part::Cylinder] Cylinder029  label="Cilindro002"
  Angle = 360
  Height = 22
  Placement = pos=(20.25,-32,125.75) rot=(0,1,0;1.5708rad)
  Radius = 3
FEATURE [Part::Cut] Cut038
  Base = -> Chamfer004
  Tool = -> Cylinder029
FEATURE [Part::Cylinder] Cylinder030  label="Cilindro003"
  Angle = 360
  Height = 22
  Placement = pos=(20.25,-34,132.75) rot=(0,1,0;1.5708rad)
  Radius = 1.25
FEATURE [Part::Cylinder] Cylinder031  label="Cilindro004"
  Angle = 360
  Height = 22
  Placement = pos=(20.25,-30,118.75) rot=(0,1,0;1.5708rad)
  Radius = 1.25
FEATURE [Part::Cylinder] Cylinder032  label="Cilindro005"
  Angle = 360
  Height = 22
  Placement = pos=(20.25,-38,124.25) rot=(0,1,0;1.5708rad)
  Radius = 1.25
FEATURE [Part::Cylinder] Cylinder033  label="Cilindro006"
  Angle = 360
  Height = 22
  Placement = pos=(20.25,-26,127.25) rot=(0,1,0;1.5708rad)
  Radius = 1.25
FEATURE [Part::MultiFuse] Fusion027
  Shapes = -> [Cylinder030,Cylinder032,Cylinder033,Cylinder031]
FEATURE [Part::Cylinder] Cylinder034  label="Cilindro007"
  Angle = 360
  Height = 22
  Placement = pos=(20.25,-34,132.75) rot=(0,1,0;1.5708rad)
  Radius = 1.25
FEATURE [Part::Cylinder] Cylinder035  label="Cilindro008"
  Angle = 360
  Height = 22
  Placement = pos=(20.25,-30,118.75) rot=(0,1,0;1.5708rad)
  Radius = 1.25
FEATURE [Part::Cylinder] Cylinder036  label="Cilindro009"
  Angle = 360
  Height = 22
  Placement = pos=(20.25,-38,124.25) rot=(0,1,0;1.5708rad)
  Radius = 1.25
FEATURE [Part::Cylinder] Cylinder037  label="Cilindro010"
  Angle = 360
  Height = 22
  Placement = pos=(20.25,-26,127.25) rot=(0,1,0;1.5708rad)
  Radius = 1.25
FEATURE [Part::MultiFuse] Fusion028
  Placement = pos=(114.108,21,33.6462) rot=(0.280624,-0.280624,-0.917878;1.65638rad)
  Shapes = -> [Cylinder034,Cylinder036,Cylinder037,Cylinder035]
FEATURE [Part::Cut] Cut039
  Base = -> Cut038
  Tool = -> Fusion028
FEATURE [Part::Cut] Cut040
  Base = -> Cut039
  Tool = -> Fusion027
FEATURE [Part::Cylinder] Cylinder038  label="Cilindro011"
  Angle = 360
  Height = 22
  Placement = pos=(-4.75,-32,125.75) rot=(0,1,0;1.5708rad)
  Radius = 1.75
FEATURE [Part::Cut] Cut041  label="shoulder-src"
  Base = -> Cut040
  Tool = -> Cylinder038
FEATURE [Part::FeaturePython] Clone008  label="microservo003"  # Draft clone (typed FeaturePython)
  Objects = -> [Clone007]
  Placement = pos=(-171,51.5,122.5) rot=(0.57735,-0.57735,0.57735;2.0944rad)
  Scale = (1,1,1)
FEATURE [Part::Box] Box026  label="Cubo004"
  Height = 56
  Length = 19
  Placement = pos=(4,98,80) rot=(0,0,1;0rad)
  Width = 15
FEATURE [Part::Cylinder] Cylinder039  label="Cilindro014"
  Angle = 360
  Height = 32
  Placement = pos=(8,90,84) rot=(-1,0,0;1.5708rad)
  Radius = 1.75
FEATURE [Part::Cylinder] Cylinder040  label="Cilindro015"
  Angle = 360
  Height = 32
  Placement = pos=(18,90,84) rot=(-1,0,0;1.5708rad)
  Radius = 1.75
FEATURE [Part::MultiFuse] Fusion029
  Shapes = -> [Cylinder040,Cylinder039]
FEATURE [Part::Cut] Cut042
  Base = -> Box026
  Tool = -> Fusion029
FEATURE [Sketcher::SketchObject] Sketch009
  Placement = pos=(38,-16,143.25) rot=(0,1,0;1.5708rad)
  sketch-geometry (7):
    g0: Circle CenterX=37 CenterY=120 CenterZ=0 NormalX=0 NormalY=0 NormalZ=1 Radius=1
    g1: Circle CenterX=9.5 CenterY=120 CenterZ=0 NormalX=0 NormalY=0 NormalZ=1 Radius=1
    g2: LineSegment StartX=35.25 StartY=126.5 StartZ=0 EndX=11.25 EndY=126.5 EndZ=0
    g3: LineSegment StartX=11.25 StartY=126.5 StartZ=0 EndX=11.25 EndY=113.5 EndZ=0
    g4: LineSegment StartX=11.25 StartY=113.5 StartZ=0 EndX=35.25 EndY=113.5 EndZ=0
    g5: LineSegment StartX=35.25 StartY=113.5 StartZ=0 EndX=35.25 EndY=126.5 EndZ=0
    g6: LineSegment [constr] StartX=9.5 StartY=120 StartZ=0 EndX=37 EndY=120 EndZ=0
  constraints (20):
    c: Coincident(g2,g3)
    c: Coincident(g3,g4)
    c: Coincident(g4,g5)
    c: Coincident(g5,g2)
    c: Horizontal(g2)
    c: Horizontal(g4)
    c: Vertical(g3)
    c: Vertical(g5)
    c: Distance(g2) = 24
    c: Distance(g5) = 13
    c: Radius(g1) = 1
    c: Equal(g1,g0)
    c: Coincident(g0,g6)
    c: Coincident(g1,g6)
    c: Distance(g6) = 27.5
    c: Horizontal(g6)
    c: DistanceX(g-1,g1) = 9.5
    c: DistanceY(g1) = 120
    c: DistanceY(g1,g3) = -6.5
    c: DistanceX(g1,g2) = 1.75
FEATURE [PartDesign::Pad] Pad004
  Length = 30
  Length2 = 100
  Placement = pos=(38,-16,143.25) rot=(0,1,0;1.5708rad)
  Reversed = true
  Sketch = -> Sketch009
  Type = 0
FEATURE [Part::Cut] Cut043
  Base = -> Cut042
  Tool = -> Pad004
FEATURE [Part::Chamfer] Chamfer005
  Base = -> Cut043
  Edges = 2 edges r=3: [Edge2,Edge14]
FEATURE [Part::Cylinder] Cylinder041  label="Cilindro016"
  Angle = 360
  Height = 32
  Placement = pos=(-5,104,125.85) rot=(-0.57735,0.57735,-0.57735;2.0944rad)
  Radius = 1.75
FEATURE [Part::Prism] Prism  label="Prisma"
  Circumradius = 3.3
  Height = 10
  Placement = pos=(6,104,125.85) rot=(-0.57735,0.57735,-0.57735;2.0944rad)
  Polygon = 6
FEATURE [Part::MultiFuse] Fusion030
  Shapes = -> [Prism,Cylinder041]
FEATURE [Part::Cut] Cut044  label="arm-src"
  Base = -> Chamfer005
  Tool = -> Fusion030
FEATURE [Part::Box] Box027  label="Cube078"
  Height = 66
  Length = 76
  Placement = pos=(-21,-2,87) rot=(0,0,1;0rad)
  Width = 76
FEATURE [Part::Fillet] Fillet007
  Base = -> Box027
  Edges = 8 edges r=3.5: [Edge1,Edge2,Edge3,Edge5,Edge6,Edge7,Edge10,Edge12]
  Placement = pos=(0,0,-24) rot=(0,0,1;0rad)
FEATURE [Part::Cylinder] Cylinder042  label="Cylinder105"
  Angle = 360
  Height = 31
  Placement = pos=(-8.5,11,71.5) rot=(1,0,0;1.5708rad)
  Radius = 1.75
FEATURE [Part::Cylinder] Cylinder043  label="Cylinder106"
  Angle = 360
  Height = 31
  Placement = pos=(-8.5,80,71.5) rot=(1,0,0;1.5708rad)
  Radius = 1.75
FEATURE [Part::Cylinder] Cylinder044  label="Cylinder107"
  Angle = 360
  Height = 31
  Placement = pos=(-4,11,83.5) rot=(1,0,0;1.5708rad)
  Radius = 6
FEATURE [Part::Box] Box028  label="Cube079"
  Height = 11
  Length = 8
  Placement = pos=(-13.5,-13,95) rot=(0,0,1;0rad)
  Width = 24
FEATURE [Part::Cylinder] Cylinder045  label="Cylinder108"
  Angle = 360
  Height = 31
  Placement = pos=(-7,80,89.6) rot=(1,0,0;1.5708rad)
  Radius = 4
FEATURE [Part::Box] Box029  label="Cube080"
  Height = 49
  Length = 17
  Placement = pos=(-14,-2.5,75) rot=(0,0,1;0rad)
  Width = 77
FEATURE [Part::Fillet] Fillet008
  Base = -> Box029
  Edges = 12 edges r=2: [Edge1,Edge2,Edge3,Edge4,Edge5,Edge6,Edge7,Edge8,Edge9,Edge10,Edge11,Edge12]
FEATURE [Part::Box] Box030  label="Cubo007"
  Height = 63
  Length = 80
  Placement = pos=(-23,-4,68) rot=(0,0,1;0rad)
  Width = 80
FEATURE [Part::Cut] Cut045
  Base = -> Box030
  Tool = -> Fillet007
FEATURE [Part::MultiFuse] Fusion031
  Shapes = -> [Box028,Cylinder044,Cylinder042,Fillet008,Cylinder045,Cylinder043]
FEATURE [Part::Cut] Cut046
  Base = -> Cut045
  Tool = -> Fusion031
FEATURE [Sketcher::SketchObject] Sketch010
  Placement = pos=(-0.25,-35,0) rot=(1,0,0;1.5708rad)
  sketch-geometry (7):
    g0: Circle CenterX=37 CenterY=120 CenterZ=0 NormalX=0 NormalY=0 NormalZ=1 Radius=1.2
    g1: Circle CenterX=9.5 CenterY=120 CenterZ=0 NormalX=0 NormalY=0 NormalZ=1 Radius=1.2
    g2: LineSegment StartX=35.25 StartY=126.5 StartZ=0 EndX=11.25 EndY=126.5 EndZ=0
    g3: LineSegment StartX=11.25 StartY=126.5 StartZ=0 EndX=11.25 EndY=113.5 EndZ=0
    g4: LineSegment StartX=11.25 StartY=113.5 StartZ=0 EndX=35.25 EndY=113.5 EndZ=0
    g5: LineSegment StartX=35.25 StartY=113.5 StartZ=0 EndX=35.25 EndY=126.5 EndZ=0
    g6: LineSegment [constr] StartX=9.5 StartY=120 StartZ=0 EndX=37 EndY=120 EndZ=0
  constraints (20):
    c: Coincident(g2,g3)
    c: Coincident(g3,g4)
    c: Coincident(g4,g5)
    c: Coincident(g5,g2)
    c: Horizontal(g2)
    c: Horizontal(g4)
    c: Vertical(g3)
    c: Vertical(g5)
    c: Distance(g2) = 24
    c: Distance(g5) = 13
    c: Radius(g1) = 1.2
    c: Equal(g1,g0)
    c: Coincident(g0,g6)
    c: Coincident(g1,g6)
    c: Distance(g6) = 27.5
    c: Horizontal(g6)
    c: DistanceX(g-1,g1) = 9.5
    c: DistanceY(g1) = 120
    c: DistanceY(g1,g3) = -6.5
    c: DistanceX(g1,g2) = 1.75
FEATURE [PartDesign::Pad] Pad005
  Length = 140
  Length2 = 100
  Placement = pos=(-0.25,-35,0) rot=(1,0,0;1.5708rad)
  Reversed = true
  Sketch = -> Sketch010
  Type = 0
FEATURE [Part::Box] Box031  label="Cubo008"
  Height = 4
  Length = 14
  Placement = pos=(11,75.5,109) rot=(0,0,1;0rad)
  Width = 3
FEATURE [Part::Box] Box032  label="Cubo009"
  Height = 4
  Length = 14
  Placement = pos=(11,75.5,127) rot=(0,0,1;0rad)
  Width = 3
FEATURE [Part::Box] Box033  label="Cubo010"
  Height = 4
  Length = 14
  Placement = pos=(11,-6.5,109) rot=(0,0,1;0rad)
  Width = 3
FEATURE [Part::Box] Box034  label="Cubo011"
  Height = 4
  Length = 14
  Placement = pos=(11,-6.5,127) rot=(0,0,1;0rad)
  Width = 3
FEATURE [Part::Cut] Cut047
  Base = -> Cut046
  Tool = -> Pad005
FEATURE [Part::MultiFuse] Fusion032
  Shapes = -> [Cut047,Box032,Box031,Box033,Box034]
FEATURE [Part::Fillet] Fillet009  label="prebody"
  Base = -> Fusion032
  Edges = 8 edges r=1: [Edge2,Edge4,Edge64,Edge66,Edge160,Edge165,Edge170,Edge174]
FEATURE [Part::FeaturePython] Clone009  label="right-shoulder"  # Draft clone (typed FeaturePython)
  Objects = -> [Cut041]
  Placement = pos=(-275,70,2.5) rot=(0,0,-1;1.5708rad)
  Scale = (1,1,1)
FEATURE [Part::Mirroring] Part__Mirroring006  label="left-shoulder"
  Base = (0,0,0)
  Normal = (0,1,0)
  Placement = pos=(-478,0,0) rot=(0,0,1;3.14159rad)
  Source = -> Clone009
FEATURE [Part::FeaturePython] Clone010  label="head-servo"  # Draft clone (typed FeaturePython)
  Objects = -> [Clone007]
  Placement = pos=(-239,46.75,151) rot=(0.707107,0.707107,0;3.14159rad)
  Scale = (1,1,1)
FEATURE [Part::Feature] Pocket005  label="shaft-drill001"
  Placement = pos=(-171,34.6,128.25) rot=(1,0,0;1.5708rad)
  shape: bbox 18.7 x 4.1 x 18.7 mm, 22 faces (baked)
FEATURE [Part::Cylinder] Cylinder046  label="Cilindro019"
  Angle = 360
  Height = 13
  Placement = pos=(17.25,-6,120) rot=(1,0,0;1.5708rad)
  Radius = 3
FEATURE [Part::Cylinder] Cylinder047  label="Cilindro020"
  Angle = 360
  Height = 22
  Placement = pos=(20.25,-34,132.75) rot=(0,1,0;1.5708rad)
  Radius = 1.25
FEATURE [Part::Cylinder] Cylinder048  label="Cilindro021"
  Angle = 360
  Height = 22
  Placement = pos=(20.25,-30,118.75) rot=(0,1,0;1.5708rad)
  Radius = 1.25
FEATURE [Part::Cylinder] Cylinder049  label="Cilindro022"
  Angle = 360
  Height = 22
  Placement = pos=(20.25,-38,124.25) rot=(0,1,0;1.5708rad)
  Radius = 1.25
FEATURE [Part::Cylinder] Cylinder050  label="Cilindro023"
  Angle = 360
  Height = 22
  Placement = pos=(20.25,-26,127.25) rot=(0,1,0;1.5708rad)
  Radius = 1.25
FEATURE [Part::MultiFuse] Fusion033
  Placement = pos=(114.108,21,33.6462) rot=(0.280624,-0.280624,-0.917878;1.65638rad)
  Shapes = -> [Cylinder047,Cylinder049,Cylinder050,Cylinder048]
FEATURE [Part::MultiFuse] Fusion034
  Placement = pos=(-256.25,172.75,144) rot=(1,0,0;1.5708rad)
  Shapes = -> [Fusion033,Cylinder046]
FEATURE [Part::Box] Box035  label="Cubo"
  Height = 4
  Length = 10
  Placement = pos=(13,-11,104) rot=(0,0,1;0rad)
  Width = 94
FEATURE [Part::Cut] Cut048  label="body-src"
  Base = -> Fillet009
  Tool = -> Box035
FEATURE [Part::FeaturePython] Clone011  label="Clone of body-src"  # Draft clone (typed FeaturePython)
  Objects = -> [Cut048]
  Placement = pos=(-275,70,2) rot=(0,0,-1;1.5708rad)
  Scale = (1,1,1)
FEATURE [Part::Cut] Cut049
  Base = -> Clone011
  Tool = -> Fusion034
FEATURE [Part::Box] Box036  label="Cubo012"
  Height = 10
  Length = 10
  Placement = pos=(-244,64,124) rot=(0,0,1;0rad)
  Width = 4
FEATURE [Part::Cut] Cut050  label="body-yaw-head"
  Base = -> Cut049
  Tool = -> Box036
FEATURE [Part::Feature] Compound  label="Servo-Futaba-3003-ready002"
  Placement = pos=(-203,69.69,14.95) rot=(0,0.707107,-0.707107;3.14159rad)
  shape: bbox 57.75 x 41.74 x 20 mm, 378 faces, 4 solids (baked)
FEATURE [Part::Feature] Chamfer006  label="ISO4762_Hex_screw-M3x020"
  Placement = pos=(-227.45,37.49,20) rot=(0.57735,0.57735,-0.57735;2.0944rad)
  shape: bbox 5.5 x 19 x 5.5 mm, 16 faces (baked)
FEATURE [Part::Feature] Chamfer007  label="ISO4762_Hex_screw-M3x023"
  Placement = pos=(-227.45,37.49,10) rot=(0.57735,0.57735,-0.57735;2.0944rad)
  shape: bbox 5.5 x 19 x 5.5 mm, 16 faces (baked)
FEATURE [Part::Feature] Chamfer008  label="ISO4032-Hex-Nut-M008"
  Placement = pos=(-227.45,48.69,10) rot=(0,0,1;0rad)
  shape: bbox 6.35 x 2.4 x 6.35 mm, 29 faces (baked)
FEATURE [Part::Feature] Chamfer009  label="ISO4032-Hex-Nut-M007"
  Placement = pos=(-227.45,48.49,20) rot=(0,0,1;0rad)
  shape: bbox 6.35 x 2.4 x 6.35 mm, 29 faces (baked)
FEATURE [Part::Feature] Chamfer010  label="ISO-10642-M3x011"
  Placement = pos=(-212.45,70.2132,15) rot=(0.57735,0.57735,-0.57735;2.0944rad)
  shape: bbox 6.046 x 10 x 6.046 mm, 25 faces (baked)
FEATURE [Part::Feature] Chamfer011  label="ISO4762_Hex_screw-M3x022"
  Placement = pos=(-178.45,37.49,20) rot=(0.57735,0.57735,-0.57735;2.0944rad)
  shape: bbox 5.5 x 19 x 5.5 mm, 16 faces (baked)
FEATURE [Part::Feature] Chamfer012  label="ISO4032-Hex-Nut-M010"
  Placement = pos=(-178.45,48.49,20) rot=(0,0,1;0rad)
  shape: bbox 6.35 x 2.4 x 6.35 mm, 29 faces (baked)
FEATURE [Part::Feature] Chamfer013  label="ISO4032-Hex-Nut-M009"
  Placement = pos=(-178.45,48.49,10) rot=(0,0,1;0rad)
  shape: bbox 6.35 x 2.4 x 6.35 mm, 29 faces (baked)
FEATURE [Part::Feature] Chamfer014  label="ISO4762_Hex_screw-M3x021"
  Placement = pos=(-178.45,37.49,10) rot=(0.57735,0.57735,-0.57735;2.0944rad)
  shape: bbox 5.5 x 19 x 5.5 mm, 16 faces (baked)
FEATURE [Part::Feature] Chamfer015  label="ISO-10642-M3x10"
  Placement = pos=(-265.35,70.0132,15) rot=(0.57735,0.57735,-0.57735;2.0944rad)
  shape: bbox 6.046 x 10 x 6.046 mm, 25 faces (baked)
FEATURE [Part::Feature] Chamfer016  label="ISO4032-Hex-Nut-M3"
  Placement = pos=(-250.35,48.29,20) rot=(0,0,1;0rad)
  shape: bbox 6.35 x 2.4 x 6.35 mm, 29 faces (baked)
FEATURE [Part::Feature] Chamfer017  label="ISO4032-Hex-Nut-M004"
  Placement = pos=(-250.35,47.69,10) rot=(0,0,1;0rad)
  shape: bbox 6.35 x 2.4 x 6.35 mm, 29 faces (baked)
FEATURE [Part::Feature] Chamfer018  label="ISO4032-Hex-Nut-M005"
  Placement = pos=(-299.35,47.69,20) rot=(0,0,1;0rad)
  shape: bbox 6.35 x 2.4 x 6.35 mm, 29 faces (baked)
FEATURE [Part::Feature] Chamfer019  label="ISO4032-Hex-Nut-M006"
  Placement = pos=(-299.35,47.69,10) rot=(0,0,1;0rad)
  shape: bbox 6.35 x 2.4 x 6.35 mm, 29 faces (baked)
FEATURE [Part::Feature] Chamfer020  label="ISO4762_Hex_screw-M3x16"
  Placement = pos=(-299.35,37.19,20) rot=(0.57735,0.57735,-0.57735;2.0944rad)
  shape: bbox 5.5 x 19 x 5.5 mm, 16 faces (baked)
FEATURE [Part::Feature] Compound001  label="Servo-Futaba-3003-ready001"
  Placement = pos=(-274.9,69.49,14.95) rot=(1,0,0;1.5708rad)
  shape: bbox 57.75 x 41.74 x 20 mm, 378 faces, 4 solids (baked)
FEATURE [Part::Feature] Chamfer021  label="ISO4762_Hex_screw-M3x017"
  Placement = pos=(-299.35,37.29,10) rot=(0.57735,0.57735,-0.57735;2.0944rad)
  shape: bbox 5.5 x 19 x 5.5 mm, 16 faces (baked)
FEATURE [Part::Feature] Chamfer022  label="ISO4762_Hex_screw-M3x018"
  Placement = pos=(-250.35,37.29,10) rot=(0.57735,0.57735,-0.57735;2.0944rad)
  shape: bbox 5.5 x 19 x 5.5 mm, 16 faces (baked)
FEATURE [Part::Feature] Chamfer023  label="ISO4762_Hex_screw-M3x019"
  Placement = pos=(-250.35,37.29,20) rot=(0.57735,0.57735,-0.57735;2.0944rad)
  shape: bbox 5.5 x 19 x 5.5 mm, 16 faces (baked)
FEATURE [Part::Feature] Fillet010  label="rounded-horn003"
  Placement = pos=(-265.45,52.9,64.75) rot=(-0.57735,0.57735,-0.57735;2.0944rad)
  shape: bbox 21 x 21 x 6.2 mm, 65 faces (baked)
FEATURE [Part::Feature] Fillet011  label="horn-screw009"
  Placement = pos=(-265.45,45.45,59.15) rot=(0,0.707107,-0.707107;3.14159rad)
  shape: bbox 4.8 x 4.8 x 5.5 mm, 21 faces (baked)
FEATURE [Part::Feature] Fillet012  label="horn-screw010"
  Placement = pos=(-272.9,55.245,59.15) rot=(0,0.707107,-0.707107;3.14159rad)
  shape: bbox 4.8 x 4.8 x 5.5 mm, 21 faces (baked)
FEATURE [Part::Feature] Fillet013  label="horn-screw011"
  Placement = pos=(-258,55.995,59.15) rot=(0,0.707107,-0.707107;3.14159rad)
  shape: bbox 4.8 x 4.8 x 5.5 mm, 21 faces (baked)
FEATURE [Part::Feature] Fillet014  label="rounded-horn002"
  Placement = pos=(-265.45,31.4,14.95) rot=(0.707107,0,-0.707107;3.14159rad)
  shape: bbox 21 x 6.2 x 21 mm, 65 faces (baked)
FEATURE [Part::Feature] Fillet015  label="horn-screw006"
  Placement = pos=(-265.45,25.8,22.4) rot=(0.707107,0,0.707107;3.14159rad)
  shape: bbox 4.8 x 5.5 x 4.8 mm, 21 faces (baked)
FEATURE [Part::Feature] Fillet016  label="horn-screw007"
  Placement = pos=(-258,25.8,11.855) rot=(0.707107,0,0.707107;3.14159rad)
  shape: bbox 4.8 x 5.5 x 4.8 mm, 21 faces (baked)
FEATURE [Part::Feature] Fillet017  label="horn-screw008"
  Placement = pos=(-272.9,25.8,11.855) rot=(0.707107,0,0.707107;3.14159rad)
  shape: bbox 4.8 x 5.5 x 4.8 mm, 21 faces (baked)
FEATURE [Part::Feature] Cut051  label="Shaft-bolt001"
  Placement = pos=(-265.402,52.9083,67.75) rot=(0.707107,-0.707107,0;3.14159rad)
  shape: bbox 5.38 x 5.38 x 9.391 mm, 18 faces (baked)
FEATURE [Part::Feature] Cut052  label="Shaft-bolt002"
  Placement = pos=(-212.402,52.9083,67.75) rot=(0.707107,-0.707107,0;3.14159rad)
  shape: bbox 5.38 x 5.38 x 9.391 mm, 18 faces (baked)
FEATURE [Part::Feature] Fillet018  label="horn-screw005"
  Placement = pos=(-219.9,26,11.855) rot=(0.707107,0,0.707107;3.14159rad)
  shape: bbox 4.8 x 5.5 x 4.8 mm, 21 faces (baked)
FEATURE [Part::Feature] Fillet019  label="horn-screw004"
  Placement = pos=(-212.45,26,22.4) rot=(0.707107,0,0.707107;3.14159rad)
  shape: bbox 4.8 x 5.5 x 4.8 mm, 21 faces (baked)
FEATURE [Part::Feature] Fillet020  label="horn-screw003"
  Placement = pos=(-205,26,11.855) rot=(0.707107,0,0.707107;3.14159rad)
  shape: bbox 4.8 x 5.5 x 4.8 mm, 21 faces (baked)
FEATURE [Part::Feature] Fillet021  label="horn-screw002"
  Placement = pos=(-219.9,55.245,59.15) rot=(0,0.707107,-0.707107;3.14159rad)
  shape: bbox 4.8 x 4.8 x 5.5 mm, 21 faces (baked)
FEATURE [Part::Feature] Fillet022  label="horn-screw001"
  Placement = pos=(-212.45,45.45,59.15) rot=(0,0.707107,-0.707107;3.14159rad)
  shape: bbox 4.8 x 4.8 x 5.5 mm, 21 faces (baked)
FEATURE [Part::Feature] Fillet023  label="horn-screw"
  Placement = pos=(-205,55.995,59.15) rot=(0,0.707107,-0.707107;3.14159rad)
  shape: bbox 4.8 x 4.8 x 5.5 mm, 21 faces (baked)
FEATURE [Part::Feature] Fillet024  label="rounded-horn001"
  Placement = pos=(-212.45,52.9,64.75) rot=(-0.57735,0.57735,-0.57735;2.0944rad)
  shape: bbox 21 x 21 x 6.2 mm, 65 faces (baked)
FEATURE [Part::Feature] Fillet025  label="rounded-horn"
  Placement = pos=(-212.45,31.6,14.95) rot=(0.707107,0,-0.707107;3.14159rad)
  shape: bbox 21 x 6.2 x 21 mm, 65 faces (baked)
FEATURE [Part::Feature] Chamfer024  label="ISO4762_Hex_screw-M3x10"
  Placement = pos=(-246,80.8,113.94) rot=(0.57735,0.57735,-0.57735;2.0944rad)
  shape: bbox 5.5 x 13 x 5.5 mm, 16 faces (baked)
FEATURE [Part::Feature] Chamfer025  label="ISO4762_Hex_screw-M3x027"
  Placement = pos=(-246,80.8,93.94) rot=(0.57735,0.57735,-0.57735;2.0944rad)
  shape: bbox 5.5 x 13 x 5.5 mm, 16 faces (baked)
FEATURE [Part::Feature] Chamfer026  label="ISO4762_Hex_screw-M3x024"
  Placement = pos=(-226,80.8,113.94) rot=(0.57735,0.57735,-0.57735;2.0944rad)
  shape: bbox 5.5 x 13 x 5.5 mm, 16 faces (baked)
FEATURE [Part::Feature] Chamfer027  label="ISO4032-Hex-Nut-M012"
  Placement = pos=(-246,87.5,113.94) rot=(0,0,1;0rad)
  shape: bbox 6.35 x 2.4 x 6.35 mm, 29 faces (baked)
FEATURE [Part::Feature] Chamfer028  label="ISO4762_Hex_screw-M3x025"
  Placement = pos=(-246,80.8,93.94) rot=(0.57735,0.57735,-0.57735;2.0944rad)
  shape: bbox 5.5 x 13 x 5.5 mm, 16 faces (baked)
FEATURE [Part::Feature] Chamfer029  label="ISO4032-Hex-Nut-M013"
  Placement = pos=(-226,87.5,93.94) rot=(0,0,1;0rad)
  shape: bbox 6.35 x 2.4 x 6.35 mm, 29 faces (baked)
FEATURE [Part::Feature] Chamfer030  label="ISO4762_Hex_screw-M3x026"
  Placement = pos=(-226,80.8,93.94) rot=(0.57735,0.57735,-0.57735;2.0944rad)
  shape: bbox 5.5 x 13 x 5.5 mm, 16 faces (baked)
FEATURE [Part::Feature] Chamfer031  label="ISO4032-Hex-Nut-M014"
  Placement = pos=(-246,87.5,93.94) rot=(0,0,1;0rad)
  shape: bbox 6.35 x 2.4 x 6.35 mm, 29 faces (baked)
FEATURE [Part::Feature] Chamfer032  label="ISO4032-Hex-Nut-M011"
  Placement = pos=(-226,87.5,113.94) rot=(0,0,1;0rad)
  shape: bbox 6.35 x 2.4 x 6.35 mm, 29 faces (baked)
FEATURE [Part::Feature] Chamfer033  label="ISO4032-Hex-Nut-M020"
  Placement = pos=(-207.5,19,77.04) rot=(0.57735,-0.57735,-0.57735;2.0944rad)
  shape: bbox 6.35 x 6.35 x 2.4 mm, 29 faces (baked)
FEATURE [Part::Feature] Chamfer034  label="ISO4762_Hex_screw-M3x033"
  Placement = pos=(-217.5,19,68.54) rot=(0.707107,-0.707107,0;3.14159rad)
  shape: bbox 5.5 x 5.5 x 15 mm, 16 faces (baked)
FEATURE [Part::Feature] Chamfer035  label="ISO4762_Hex_screw-M3x030"
  Placement = pos=(-270.5,68,68.54) rot=(0.707107,-0.707107,0;3.14159rad)
  shape: bbox 5.5 x 5.5 x 15 mm, 16 faces (baked)
FEATURE [Part::Feature] Chamfer036  label="ISO4762_Hex_screw-M3x031"
  Placement = pos=(-217.5,68,68.54) rot=(0.707107,-0.707107,0;3.14159rad)
  shape: bbox 5.5 x 5.5 x 15 mm, 16 faces (baked)
FEATURE [Part::Feature] Chamfer037  label="ISO4762_Hex_screw-M3x032"
  Placement = pos=(-207.5,68,68.54) rot=(0.707107,-0.707107,0;3.14159rad)
  shape: bbox 5.5 x 5.5 x 15 mm, 16 faces (baked)
FEATURE [Part::Feature] Chamfer038  label="ISO4032-Hex-Nut-M019"
  Placement = pos=(-217.5,19,77.04) rot=(0.57735,-0.57735,-0.57735;2.0944rad)
  shape: bbox 6.35 x 6.35 x 2.4 mm, 29 faces (baked)
FEATURE [Part::Feature] Chamfer039  label="ISO4762_Hex_screw-M3x029"
  Placement = pos=(-260.5,68,68.54) rot=(0.707107,-0.707107,0;3.14159rad)
  shape: bbox 5.5 x 5.5 x 15 mm, 16 faces (baked)
FEATURE [Part::Feature] Chamfer040  label="ISO4032-Hex-Nut-M018"
  Placement = pos=(-270.5,19,77.04) rot=(0.57735,-0.57735,-0.57735;2.0944rad)
  shape: bbox 6.35 x 6.35 x 2.4 mm, 29 faces (baked)
FEATURE [Part::Feature] Chamfer041  label="ISO4762_Hex_screw-M3x12"
  Placement = pos=(-270.5,19,68.54) rot=(0.707107,-0.707107,0;3.14159rad)
  shape: bbox 5.5 x 5.5 x 15 mm, 16 faces (baked)
FEATURE [Part::Feature] Chamfer042  label="ISO4032-Hex-Nut-M017"
  Placement = pos=(-260.5,68,77.04) rot=(0.57735,-0.57735,-0.57735;2.0944rad)
  shape: bbox 6.35 x 6.35 x 2.4 mm, 29 faces (baked)
FEATURE [Part::Feature] Chamfer043  label="ISO4032-Hex-Nut-M023"
  Placement = pos=(-272,78.5,73.94) rot=(0,0,-1;1.5708rad)
  shape: bbox 2.4 x 6.35 x 6.35 mm, 29 faces (baked)
FEATURE [Part::Feature] Chamfer044  label="ISO4762_Hex_screw-M3x028"
  Placement = pos=(-260.5,19,68.54) rot=(0.707107,-0.707107,0;3.14159rad)
  shape: bbox 5.5 x 5.5 x 15 mm, 16 faces (baked)
FEATURE [Part::Feature] Chamfer045  label="ISO4032-Hex-Nut-M022"
  Placement = pos=(-217.5,68,77.04) rot=(0.57735,-0.57735,-0.57735;2.0944rad)
  shape: bbox 6.35 x 6.35 x 2.4 mm, 29 faces (baked)
FEATURE [Part::Feature] Chamfer046  label="ISO4032-Hex-Nut-M021"
  Placement = pos=(-207.5,68,77.04) rot=(0.57735,-0.57735,-0.57735;2.0944rad)
  shape: bbox 6.35 x 6.35 x 2.4 mm, 29 faces (baked)
FEATURE [Part::Feature] Compound002  label="Servo-Futaba-3003-ready003"
  Placement = pos=(-265.45,43.45,102.84) rot=(0.707107,0.707107,0;3.14159rad)
  shape: bbox 20 x 57.75 x 41.74 mm, 378 faces, 4 solids (baked)
FEATURE [Part::Feature] Chamfer047  label="ISO4032-Hex-Nut-M015"
  Placement = pos=(-260.5,19,77.04) rot=(0.57735,-0.57735,-0.57735;2.0944rad)
  shape: bbox 6.35 x 6.35 x 2.4 mm, 29 faces (baked)
FEATURE [Part::Feature] Compound003  label="Servo-Futaba-3003-ready004"
  Placement = pos=(-212.45,43.45,102.84) rot=(0.707107,0.707107,0;3.14159rad)
  shape: bbox 20 x 57.75 x 41.74 mm, 378 faces, 4 solids (baked)
FEATURE [Part::Feature] Chamfer048  label="ISO4762_Hex_screw-M3x034"
  Placement = pos=(-207.5,19,68.54) rot=(0.707107,-0.707107,0;3.14159rad)
  shape: bbox 5.5 x 5.5 x 15 mm, 16 faces (baked)
FEATURE [Part::Feature] Chamfer049  label="ISO4032-Hex-Nut-M016"
  Placement = pos=(-270.5,68,77.04) rot=(0.57735,-0.57735,-0.57735;2.0944rad)
  shape: bbox 6.35 x 6.35 x 2.4 mm, 29 faces (baked)
FEATURE [Part::Feature] Chamfer050  label="ISO4032-Hex-Nut-M024"
  Placement = pos=(-208.2,78.5,73.94) rot=(0,0,-1;1.5708rad)
  shape: bbox 2.4 x 6.35 x 6.35 mm, 29 faces (baked)
FEATURE [Part::Feature] Chamfer051  label="ISO4762_Hex_screw-M3x035"
  Placement = pos=(-307,70.9,128.25) rot=(-1,0,0;1.5708rad)
  shape: bbox 5.5 x 13 x 5.5 mm, 16 faces (baked)
FEATURE [Part::Feature] Chamfer052  label="ISO4762_Hex_screw-M3x036"
  Placement = pos=(-278.9,78.5,73.94) rot=(0.57735,0.57735,-0.57735;4.18879rad)
  shape: bbox 13 x 5.5 x 5.5 mm, 16 faces (baked)
FEATURE [Part::Feature] Pocket006  label="shaft-drill003"
  Placement = pos=(-239,52.75,134.5) rot=(0,1,0;3.14159rad)
  shape: bbox 18.7 x 18.7 x 4.1 mm, 22 faces (baked)
FEATURE [Part::Feature] Pocket007  label="shaft-drill004"
  Placement = pos=(-307,34.6,128.25) rot=(1,0,0;1.5708rad)
  shape: bbox 18.7 x 4.1 x 18.7 mm, 22 faces (baked)
FEATURE [Part::Feature] Chamfer053  label="ISO4762_Hex_screw-M3x037"
  Placement = pos=(-199.1,78.5,73.94) rot=(-0.57735,0.57735,-0.57735;2.0944rad)
  shape: bbox 13 x 5.5 x 5.5 mm, 16 faces (baked)
FEATURE [Part::Feature] Chamfer054  label="ISO4032-Hex-Nut-M025"
  Placement = pos=(-171,61.5,128.25) rot=(0,1,0;0.523599rad)
  shape: bbox 6.35 x 2.4 x 6.35 mm, 29 faces (baked)
FEATURE [Part::Feature] Fillet026  label="horn-screw012"
  Placement = pos=(-173,29,121.25) rot=(0.707107,0,0.707107;3.14159rad)
  shape: bbox 4.8 x 5.5 x 4.8 mm, 21 faces (baked)
FEATURE [Part::Feature] Fillet027  label="horn-screw013"
  Placement = pos=(-169,29,135.25) rot=(0.707107,0,0.707107;3.14159rad)
  shape: bbox 4.8 x 5.5 x 4.8 mm, 21 faces (baked)
FEATURE [Part::Feature] Fillet028  label="horn-screw014"
  Placement = pos=(-171,45.2,108.7) rot=(0.707107,0,0.707107;3.14159rad)
  shape: bbox 4.8 x 5.5 x 4.8 mm, 21 faces (baked)
FEATURE [Part::Feature] Fillet029  label="horn-screw015"
  Placement = pos=(-165,29,126.75) rot=(0.707107,0,0.707107;3.14159rad)
  shape: bbox 4.8 x 5.5 x 4.8 mm, 21 faces (baked)
FEATURE [Part::Feature] Fillet030  label="horn-screw016"
  Placement = pos=(-171,45.2,136.3) rot=(0.707107,0,0.707107;3.14159rad)
  shape: bbox 4.8 x 5.5 x 4.8 mm, 21 faces (baked)
FEATURE [Part::Feature] Fillet031  label="horn-screw017"
  Placement = pos=(-177,29,129.75) rot=(0.707107,0,0.707107;3.14159rad)
  shape: bbox 4.8 x 5.5 x 4.8 mm, 21 faces (baked)
FEATURE [Part::Feature] Fillet032  label="horn-screw018"
  Placement = pos=(-234.854,48.1478,131) rot=(-1,0,0;1.5708rad)
  shape: bbox 4.8 x 4.8 x 5.5 mm, 21 faces (baked)
FEATURE [Part::Feature] Fillet033  label="horn-screw019"
  Placement = pos=(-307,45.2,108.7) rot=(0.707107,0,0.707107;3.14159rad)
  shape: bbox 4.8 x 5.5 x 4.8 mm, 21 faces (baked)
FEATURE [Part::Feature] Fillet034  label="horn-screw020"
  Placement = pos=(-309,29,135.25) rot=(0.707107,0,0.707107;3.14159rad)
  shape: bbox 4.8 x 5.5 x 4.8 mm, 21 faces (baked)
FEATURE [Part::Feature] Fillet035  label="horn-screw021"
  Placement = pos=(-305,29,121.25) rot=(0.707107,0,0.707107;3.14159rad)
  shape: bbox 4.8 x 5.5 x 4.8 mm, 21 faces (baked)
FEATURE [Part::Feature] Fillet036  label="horn-screw022"
  Placement = pos=(-244.562,48.0616,131) rot=(-1,0,0;1.5708rad)
  shape: bbox 4.8 x 4.8 x 5.5 mm, 21 faces (baked)
FEATURE [Part::Feature] Fillet037  label="horn-screw023"
  Placement = pos=(-233.417,57.4313,131) rot=(-1,0,0;1.5708rad)
  shape: bbox 4.8 x 4.8 x 5.5 mm, 21 faces (baked)
FEATURE [Part::Feature] Fillet038  label="horn-screw024"
  Placement = pos=(-301,29,129.75) rot=(0.707107,0,0.707107;3.14159rad)
  shape: bbox 4.8 x 5.5 x 4.8 mm, 21 faces (baked)
FEATURE [Part::Feature] Fillet039  label="horn-screw025"
  Placement = pos=(-307,45.2,136.3) rot=(0.707107,0,0.707107;3.14159rad)
  shape: bbox 4.8 x 5.5 x 4.8 mm, 21 faces (baked)
FEATURE [Part::Feature] Fillet040  label="horn-screw026"
  Placement = pos=(-313,29,126.75) rot=(0.707107,0,0.707107;3.14159rad)
  shape: bbox 4.8 x 5.5 x 4.8 mm, 21 faces (baked)
FEATURE [Part::Feature] Fillet041  label="horn-screw027"
  Placement = pos=(-243.125,57.3452,131) rot=(-1,0,0;1.5708rad)
  shape: bbox 4.8 x 4.8 x 5.5 mm, 21 faces (baked)
FEATURE [Part::Feature] Pocket008  label="shaft-drill005"
  Placement = pos=(-190.8,52.75,122.5) rot=(0,1,0;1.5708rad)
  shape: bbox 4.1 x 18.7 x 18.7 mm, 22 faces (baked)
FEATURE [Part::Feature] Pocket009  label="shaft-drill006"
  Placement = pos=(-287.2,52.75,122.5) rot=(0,-1,0;1.5708rad)
  shape: bbox 4.1 x 18.7 x 18.7 mm, 22 faces (baked)
FEATURE [Part::Feature] Fillet042  label="horn-screw028"
  Placement = pos=(-291.882,58.3121,127.188) rot=(0,0,1;1.5708rad)
  shape: bbox 5.5 x 4.8 x 4.8 mm, 21 faces (baked)
FEATURE [Part::Feature] Fillet043  label="horn-screw029"
  Placement = pos=(-291.882,56.8751,117.905) rot=(0,0,1;1.5708rad)
  shape: bbox 5.5 x 4.8 x 4.8 mm, 21 faces (baked)
FEATURE [Part::Feature] Fillet044  label="horn-screw030"
  Placement = pos=(-279,33.25,122) rot=(0,0,1;1.5708rad)
  shape: bbox 5.5 x 4.8 x 4.8 mm, 21 faces (baked)
FEATURE [Part::Feature] Fillet045  label="horn-screw031"
  Placement = pos=(-291.882,47.1673,117.819) rot=(0,0,1;1.5708rad)
  shape: bbox 5.5 x 4.8 x 4.8 mm, 21 faces (baked)
FEATURE [Part::Feature] Fillet046  label="horn-screw032"
  Placement = pos=(-199,60.75,122) rot=(0,0,-1;1.5708rad)
  shape: bbox 5.5 x 4.8 x 4.8 mm, 21 faces (baked)
FEATURE [Part::Feature] Fillet047  label="horn-screw033"
  Placement = pos=(-186.118,56.8751,117.905) rot=(0,0,-1;1.5708rad)
  shape: bbox 5.5 x 4.8 x 4.8 mm, 21 faces (baked)
FEATURE [Part::Feature] Fillet048  label="horn-screw034"
  Placement = pos=(-186.118,47.1673,117.819) rot=(0,0,-1;1.5708rad)
  shape: bbox 5.5 x 4.8 x 4.8 mm, 21 faces (baked)
FEATURE [Part::Feature] Fillet049  label="horn-screw035"
  Placement = pos=(-186.118,48.6043,127.102) rot=(0,0,-1;1.5708rad)
  shape: bbox 5.5 x 4.8 x 4.8 mm, 21 faces (baked)
FEATURE [Part::Feature] Fillet050  label="horn-screw036"
  Placement = pos=(-199,33.25,122) rot=(0,0,-1;1.5708rad)
  shape: bbox 5.5 x 4.8 x 4.8 mm, 21 faces (baked)
FEATURE [Part::Feature] Fillet051  label="horn-screw037"
  Placement = pos=(-186.118,58.3121,127.188) rot=(0,0,-1;1.5708rad)
  shape: bbox 5.5 x 4.8 x 4.8 mm, 21 faces (baked)
FEATURE [Part::Feature] Fillet052  label="horn-screw038"
  Placement = pos=(-279,60.75,122) rot=(0,0,1;1.5708rad)
  shape: bbox 5.5 x 4.8 x 4.8 mm, 21 faces (baked)
FEATURE [Part::Feature] Fillet053  label="horn-screw039"
  Placement = pos=(-291.882,48.6043,127.102) rot=(0,0,1;1.5708rad)
  shape: bbox 5.5 x 4.8 x 4.8 mm, 21 faces (baked)
FEATURE [Part::Feature] Chamfer055  label="ISO4762_Hex_screw-M3x038"
  Placement = pos=(-171,71,128.25) rot=(-1,0,0;1.5708rad)
  shape: bbox 5.5 x 13 x 5.5 mm, 16 faces (baked)
FEATURE [Part::Feature] Pocket010  label="top-cross001"
  Placement = pos=(-283.6,52.75,122.5) rot=(0,-1,0;1.5708rad)
  shape: bbox 6.2 x 3 x 3 mm, 18 faces (baked)
FEATURE [Part::Feature] Pocket011  label="top-cross002"
  Placement = pos=(-171,38.2,128.25) rot=(1,0,0;1.5708rad)
  shape: bbox 3 x 6.2 x 3 mm, 18 faces (baked)
FEATURE [Part::Feature] Pocket012  label="top-cross003"
  Placement = pos=(-194.4,52.75,122.5) rot=(0,1,0;1.5708rad)
  shape: bbox 6.2 x 3 x 3 mm, 18 faces (baked)
FEATURE [Part::Feature] Pocket013  label="top-cross004"
  Placement = pos=(-239,52.75,138.1) rot=(1,0,0;3.14159rad)
  shape: bbox 3 x 3 x 6.2 mm, 18 faces (baked)
FEATURE [Part::Feature] Pocket014  label="top-cross005"
  Placement = pos=(-307,38.2,128.25) rot=(1,0,0;1.5708rad)
  shape: bbox 3 x 6.2 x 3 mm, 18 faces (baked)
FEATURE [App::DocumentObjectGroup] Grupo001  label="generic-components"
  Group = -> [Compound,Chamfer006,Chamfer007,Chamfer008,Chamfer009,Chamfer010,Chamfer011,Chamfer012,Chamfer013,Chamfer014,Chamfer015,Chamfer016,Chamfer017,Chamfer018,Chamfer019,Chamfer020,Compound001,Chamfer021,Chamfer022,Chamfer023,Fillet010,Fillet011,Fillet012,Fillet013,Fillet014,Fillet015,Fillet016,Fillet017,Cut051,Cut052,Fillet018,Fillet019,Fillet020,Fillet021,Fillet022,Fillet023,Fillet024,Fillet025,+77 more]
FEATURE [Part::Feature] Cut053  label="pie-D001"
  Placement = pos=(-274.85,69.19,3) rot=(0,0,-1;1.5708rad)
  shape: bbox 58 x 72 x 24 mm, 84 faces (baked)
FEATURE [Part::Feature] Part__Mirroring007  label="pie-I001"
  Placement = pos=(-202.95,69.39,2) rot=(0,0,-1;1.5708rad)
  shape: bbox 58 x 72 x 24 mm, 84 faces (baked)
FEATURE [Sketcher::SketchObject] Sketch011
  Placement = pos=(70,275,66) rot=(0.707107,0.707107,0;3.14159rad)
  sketch-geometry (20):
    g0: LineSegment StartX=-270.5 StartY=-17 StartZ=0 EndX=-260.5 EndY=-17 EndZ=0
    g1: LineSegment StartX=-260.5 StartY=-17 StartZ=0 EndX=-260.5 EndY=-21 EndZ=0
    g2: LineSegment StartX=-260.5 StartY=-21 StartZ=0 EndX=-270.5 EndY=-21 EndZ=0
    g3: LineSegment StartX=-270.5 StartY=-21 StartZ=0 EndX=-270.5 EndY=-17 EndZ=0
    g4: LineSegment StartX=-217.5 StartY=-17 StartZ=0 EndX=-207.5 EndY=-17 EndZ=0
    g5: LineSegment StartX=-207.5 StartY=-17 StartZ=0 EndX=-207.5 EndY=-21 EndZ=0
    g6: LineSegment StartX=-207.5 StartY=-21 StartZ=0 EndX=-217.5 EndY=-21 EndZ=0
    g7: LineSegment StartX=-217.5 StartY=-21 StartZ=0 EndX=-217.5 EndY=-17 EndZ=0
    g8: LineSegment StartX=-270.5 StartY=-66 StartZ=0 EndX=-260.5 EndY=-66 EndZ=0
    g9: LineSegment StartX=-260.5 StartY=-66 StartZ=0 EndX=-260.5 EndY=-70 EndZ=0
    g10: LineSegment StartX=-260.5 StartY=-70 StartZ=0 EndX=-270.5 EndY=-70 EndZ=0
    g11: LineSegment StartX=-270.5 StartY=-70 StartZ=0 EndX=-270.5 EndY=-66 EndZ=0
    g12: LineSegment StartX=-217.5 StartY=-66 StartZ=0 EndX=-207.5 EndY=-66 EndZ=0
    g13: LineSegment StartX=-207.5 StartY=-66 StartZ=0 EndX=-207.5 EndY=-70 EndZ=0
    g14: LineSegment StartX=-207.5 StartY=-70 StartZ=0 EndX=-217.5 EndY=-70 EndZ=0
    g15: LineSegment StartX=-217.5 StartY=-70 StartZ=0 EndX=-217.5 EndY=-66 EndZ=0
    g16: LineSegment [constr] StartX=-260.5 StartY=-21 StartZ=0 EndX=-217.5 EndY=-21 EndZ=0
    g17: LineSegment [constr] StartX=-217.5 StartY=-21 StartZ=0 EndX=-217.5 EndY=-66 EndZ=0
    g18: LineSegment [constr] StartX=-217.5 StartY=-66 StartZ=0 EndX=-260.5 EndY=-66 EndZ=0
    g19: LineSegment [constr] StartX=-260.5 StartY=-66 StartZ=0 EndX=-260.5 EndY=-21 EndZ=0
  constraints (56):
    c: Coincident(g0,g1)
    c: Coincident(g1,g2)
    c: Coincident(g2,g3)
    c: Coincident(g3,g0)
    c: Horizontal(g0)
    c: Horizontal(g2)
    c: Vertical(g1)
    c: Vertical(g3)
    c: Coincident(g4,g5)
    c: Coincident(g5,g6)
    c: Coincident(g6,g7)
    c: Coincident(g7,g4)
    c: Horizontal(g4)
    c: Horizontal(g6)
    c: Vertical(g5)
    c: Vertical(g7)
    c: Coincident(g8,g9)
    c: Coincident(g9,g10)
    c: Coincident(g10,g11)
    c: Coincident(g11,g8)
    c: Horizontal(g8)
    c: Horizontal(g10)
    c: Vertical(g9)
    c: Vertical(g11)
    c: Coincident(g12,g13)
    c: Coincident(g13,g14)
    c: Coincident(g14,g15)
    c: Coincident(g15,g12)
    c: Horizontal(g12)
    c: Horizontal(g14)
    c: Vertical(g13)
    c: Vertical(g15)
    c: Equal(g15,g9)
    c: Equal(g9,g1)
    c: Equal(g1,g7)
    c: Distance(g3) = 4
    c: Distance(g0) = 10
    c: Equal(g2,g6)
    c: Equal(g6,g8)
    c: Equal(g8,g12)
    c: Coincident(g16,g17)
    c: Coincident(g17,g18)
    c: Coincident(g18,g19)
    c: Coincident(g19,g16)
    c: Horizontal(g16)
    c: Horizontal(g18)
    c: Vertical(g17)
    c: Vertical(g19)
    c: Coincident(g1,g16)
    c: Coincident(g16,g6)
    c: Coincident(g12,g17)
    c: Coincident(g18,g8)
    c: Distance(g18) = 43
    c: Distance(g17) = 45
    c: DistanceX(g-1,g6) = -217.5
    c: DistanceY(g-1,g6) = -21
FEATURE [PartDesign::Pad] Pad006
  Length = 10
  Length2 = 100
  Placement = pos=(70,275,66) rot=(0.707107,0.707107,0;3.14159rad)
  Sketch = -> Sketch011
  Type = 0
FEATURE [Part::Cut] Cut054  label="chassis-src"
  Base = -> Fillet006
  Placement = pos=(-275,70,2) rot=(0,0,-1;1.5708rad)
  Tool = -> Pad006
FEATURE [Part::FeaturePython] Clone012  label="Clone of chassis-src"  # Draft clone (typed FeaturePython)
  Objects = -> [Cut054]
  Placement = pos=(-275,70,2) rot=(0,0,-1;1.5708rad)
  Scale = (1,1,1)
FEATURE [Sketcher::SketchObject] Sketch012
  Placement = pos=(-119,23.5,141) rot=(0,0,1;1.5708rad)
  sketch-geometry (7):
    g0: Circle CenterX=37 CenterY=120 CenterZ=0 NormalX=0 NormalY=0 NormalZ=1 Radius=1.2
    g1: Circle CenterX=9.5 CenterY=120 CenterZ=0 NormalX=0 NormalY=0 NormalZ=1 Radius=1.2
    g2: LineSegment StartX=35.25 StartY=126.5 StartZ=0 EndX=11.25 EndY=126.5 EndZ=0
    g3: LineSegment StartX=11.25 StartY=126.5 StartZ=0 EndX=11.25 EndY=113.5 EndZ=0
    g4: LineSegment StartX=11.25 StartY=113.5 StartZ=0 EndX=35.25 EndY=113.5 EndZ=0
    g5: LineSegment StartX=35.25 StartY=113.5 StartZ=0 EndX=35.25 EndY=126.5 EndZ=0
    g6: LineSegment [constr] StartX=9.5 StartY=120 StartZ=0 EndX=37 EndY=120 EndZ=0
  constraints (20):
    c: Coincident(g2,g3)
    c: Coincident(g3,g4)
    c: Coincident(g4,g5)
    c: Coincident(g5,g2)
    c: Horizontal(g2)
    c: Horizontal(g4)
    c: Vertical(g3)
    c: Vertical(g5)
    c: Distance(g2) = 24
    c: Distance(g5) = 13
    c: Radius(g1) = 1.2
    c: Equal(g1,g0)
    c: Coincident(g0,g6)
    c: Coincident(g1,g6)
    c: Distance(g6) = 27.5
    c: Horizontal(g6)
    c: DistanceX(g-1,g1) = 9.5
    c: DistanceY(g1) = 120
    c: DistanceY(g1,g3) = -6.5
    c: DistanceX(g1,g2) = 1.75
FEATURE [PartDesign::Pad] Pad007
  Length = 16
  Length2 = 100
  Placement = pos=(-119,23.5,141) rot=(0,0,1;1.5708rad)
  Sketch = -> Sketch012
  Type = 0
FEATURE [Part::Box] Box037  label="Cubo013"
  Height = 15.5
  Length = 14
  Placement = pos=(-246,30,131) rot=(0,0,1;0rad)
  Width = 33.5
FEATURE [Part::Box] Box038  label="Cubo014"
  Height = 29.5
  Length = 14
  Placement = pos=(-246,34.75,132) rot=(0,0,1;0rad)
  Width = 24
FEATURE [Sketcher::SketchObject] Sketch013
  Placement = pos=(-232,0,0) rot=(0.57735,0.57735,0.57735;2.0944rad)
  sketch-geometry (12):
    g0: LineSegment StartX=58.7463 StartY=151.629 StartZ=0 EndX=56.7806 EndY=151.629 EndZ=0
    g1: LineSegment StartX=56.7806 StartY=151.629 StartZ=0 EndX=56.7806 EndY=160.733 EndZ=0
    g2: LineSegment StartX=56.7806 StartY=160.733 StartZ=0 EndX=58.7463 EndY=160.733 EndZ=0
    g3: LineSegment StartX=59.4575 StartY=151.357 StartZ=0 EndX=64.2177 EndY=147.084 EndZ=0
    g4: LineSegment StartX=70.0652 StartY=146.486 StartZ=0 EndX=68.6741 EndY=152.764 EndZ=0
    g5: ArcOfCircle CenterX=58.7463 CenterY=150.564 CenterZ=0 NormalX=0 NormalY=0 NormalZ=1 Radius=10.1685 StartAngle=0.218051 EndAngle=1.5708
    g6: ArcOfCircle CenterX=58.7463 CenterY=150.564 CenterZ=0 NormalX=0 NormalY=0 NormalZ=1 Radius=1.06462 StartAngle=0.839342 EndAngle=1.5708
    g7: LineSegment StartX=65.069 StartY=145.176 StartZ=0 EndX=65.069 EndY=134.871 EndZ=0
    g8: LineSegment StartX=65.069 StartY=134.871 StartZ=0 EndX=70.2829 EndY=134.871 EndZ=0
    g9: LineSegment StartX=70.2829 StartY=134.871 StartZ=0 EndX=70.2829 EndY=144.497 EndZ=0
    g10: ArcOfCircle CenterX=61.0884 CenterY=144.497 CenterZ=0 NormalX=0 NormalY=0 NormalZ=1 Radius=9.19448 StartAngle=0 EndAngle=0.218051
    g11: ArcOfCircle CenterX=62.5052 CenterY=145.176 CenterZ=0 NormalX=0 NormalY=0 NormalZ=1 Radius=2.56379 StartAngle=0 EndAngle=0.839342
  constraints (24):
    c: Horizontal(g0)
    c: Coincident(g0,g1)
    c: Vertical(g1)
    c: Coincident(g1,g2)
    c: Horizontal(g2)
    c: Coincident(g5,g2)
    c: Coincident(g5,g4)
    c: Coincident(g6,g0)
    c: Coincident(g6,g3)
    c: Tangent(g2,g5)
    c: Equal(g0,g6)
    c: Tangent(g5,g4)
    c: Coincident(g5,g6)
    c: Tangent(g6,g3)
    c: Tangent(g6,g0)
    c: Vertical(g7)
    c: Coincident(g7,g8)
    c: Horizontal(g8)
    c: Coincident(g8,g9)
    c: Vertical(g9)
    c: Tangent(g4,g10) = -1.5708
    c: Tangent(g9,g10) = -1.5708
    c: Tangent(g3,g11) = 1.5708
    c: Tangent(g7,g11) = 1.5708
FEATURE [PartDesign::Pad] Pad008
  Length = 14
  Length2 = 100
  Placement = pos=(-232,0,0) rot=(0.57735,0.57735,0.57735;2.0944rad)
  Reversed = true
  Sketch = -> Sketch013
  Type = 0
FEATURE [Part::MultiFuse] Fusion035  label="head-positive-cut"
  Shapes = -> [Box037,Pad008,Pad007,Box038]
FEATURE [Part::Box] Box039  label="Cubo015"
  Height = 7.5
  Length = 5
  Placement = pos=(9,97,127) rot=(0,0,1;0rad)
  Width = 12
FEATURE [Part::Cut] Cut055
  Base = -> Cut044
  Tool = -> Box039
FEATURE [App::DocumentObjectGroup] Grupo  label="src001"
  Group = -> [Cut041,Cut048,Fusion026,Cut054,Cut055]
FEATURE [App::DocumentObjectGroup] Group001  label="original-src"
  Group = -> [Part__Mirroring004,Part__Mirroring005,Group002,Group003,Grupo]
FEATURE [Part::Fillet] Fillet054
  Base = -> Cut055
  Edges = 1 edges r=0.5: [Edge83]
FEATURE [Part::FeaturePython] Clone013  label="Clone of arm"  # Draft clone (typed FeaturePython)
  Objects = -> [Fillet054]
  Placement = pos=(-275,70,2.5) rot=(0,0,-1;1.5708rad)
  Scale = (1,1,1)
FEATURE [Part::Mirroring] Part__Mirroring008  label="Clone of arm001"
  Base = (0,0,0)
  Normal = (1,0,0)
  Placement = pos=(-478,0,0) rot=(0,0,1;0rad)
  Source = -> Clone013
FEATURE [Part::Prism] Prism001  label="Prisma001"
  Circumradius = 3.3
  Height = 10
  Placement = pos=(18,85,84) rot=(-1,0,0;1.5708rad)
  Polygon = 6
FEATURE [Part::Prism] Prism002  label="Prisma002"
  Circumradius = 3.3
  Height = 10
  Placement = pos=(8,85,84) rot=(-1,0,0;1.5708rad)
  Polygon = 6
FEATURE [Part::Cylinder] Cylinder051  label="Cilindro017"
  Angle = 360
  Height = 32
  Placement = pos=(18,116,84) rot=(-1,0,0;1.5708rad)
  Radius = 3
FEATURE [Part::Cylinder] Cylinder052  label="Cilindro018"
  Angle = 360
  Height = 32
  Placement = pos=(8,116,84) rot=(-1,0,0;1.5708rad)
  Radius = 3
FEATURE [Part::Box] Box040  label="Cubo005"
  Height = 28
  Length = 20
  Placement = pos=(3.5,97.5,79.5) rot=(0,0,1;0rad)
  Width = 16
FEATURE [Part::Cylinder] Cylinder053  label="Cilindro013"
  Angle = 360
  Height = 32
  Placement = pos=(18,90,84) rot=(-1,0,0;1.5708rad)
  Radius = 1.75
FEATURE [Part::Cylinder] Cylinder054  label="Cilindro012"
  Angle = 360
  Height = 32
  Placement = pos=(8,90,84) rot=(-1,0,0;1.5708rad)
  Radius = 1.75
FEATURE [Part::MultiFuse] Fusion036  label="arm-positive-cut"
  Shapes = -> [Prism001,Prism002,Cylinder051,Cylinder052,Box040,Cylinder053,Cylinder054]
FEATURE [Part::FeaturePython] Clone014  label="Clone of arm-positive-cut-left"  # Draft clone (typed FeaturePython)
  Objects = -> [Fusion036]
  Placement = pos=(-275,70,2.8) rot=(0,0,-1;1.5708rad)
  Scale = (1,1,1)
FEATURE [Part::Mirroring] Part__Mirroring009  label="Clone of arm-positive-cut-right"
  Base = (0,0,0)
  Normal = (1,0,0)
  Placement = pos=(-478,0,0) rot=(0,0,1;0rad)
  Source = -> Clone014
FEATURE [Part::Feature] Part__Mirroring010  label="pata-I001"
  Placement = pos=(-202.95,69.9,1.95) rot=(0,0,-1;1.5708rad)
  shape: bbox 21 x 53 x 59.5 mm, 32 faces (baked)
FEATURE [Part::Feature] Part__Mirroring011  label="leg-body"
  Placement = pos=(-255.95,69.7,1.95) rot=(0,0,-1;1.5708rad)
  shape: bbox 21 x 53 x 59.5 mm, 32 faces (baked)
FEATURE [App::DocumentObjectGroup] Group006  label="Assembly"
  Group = -> [Fusion025,Part__Mirroring006,Part__Mirroring008,Part__Mirroring011,Part__Mirroring010,Part__Mirroring007,Cut053,Clone012]
FEATURE [Mesh::Feature] head
FEATURE [Mesh::Feature] body
  Placement = pos=(-281.5,0,0) rot=(0,0,1;0rad)
FEATURE [Mesh::Feature] headwithneck
  Placement = pos=(0,0,8) rot=(0,0,1;0rad)
